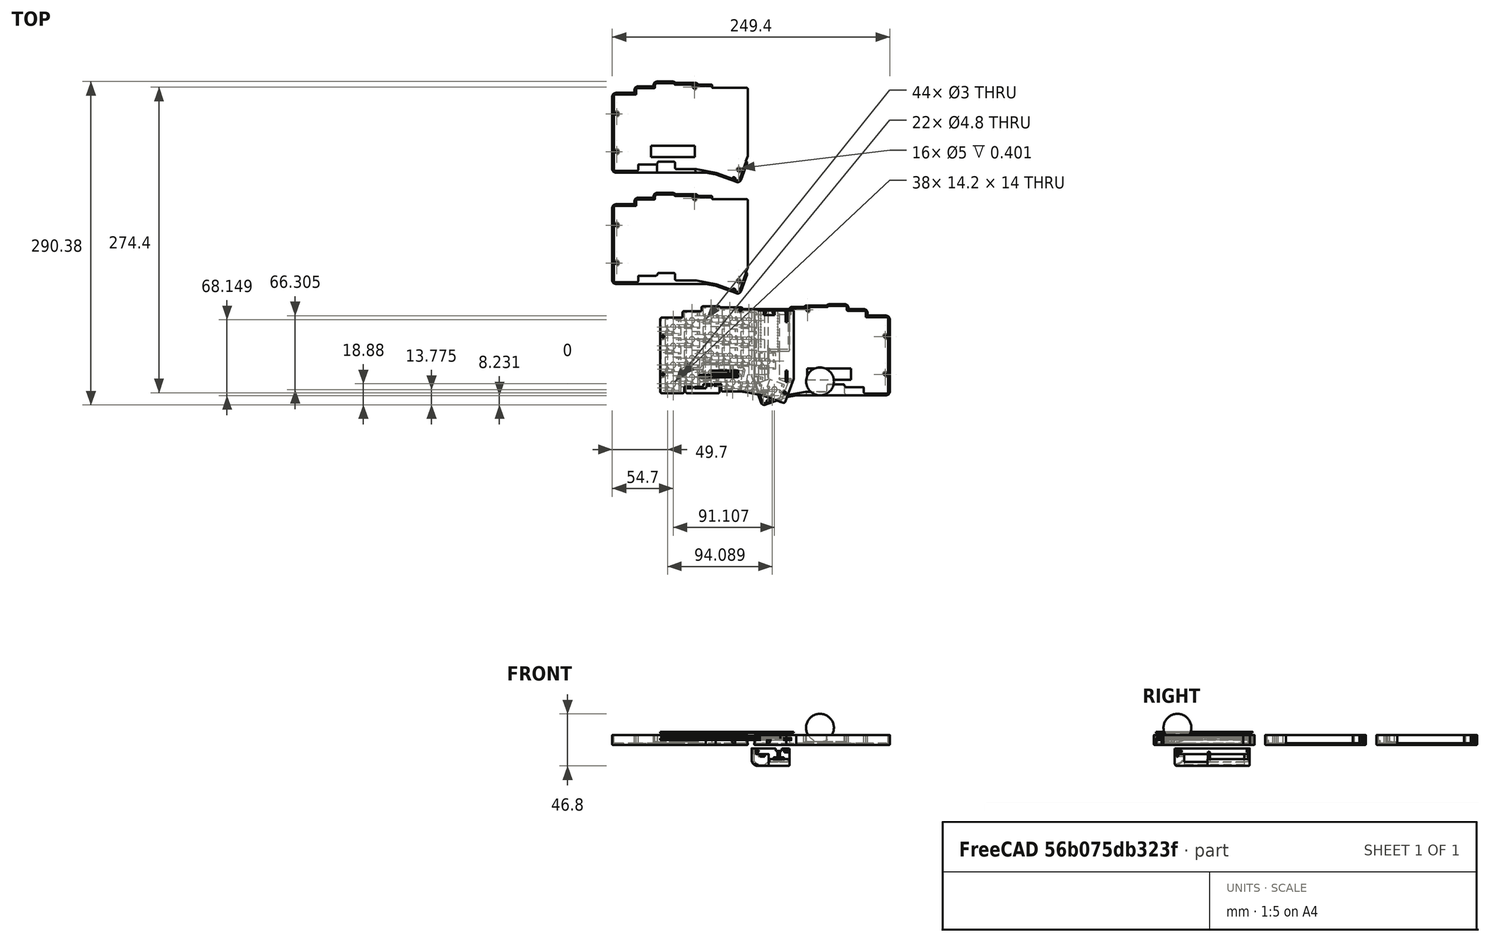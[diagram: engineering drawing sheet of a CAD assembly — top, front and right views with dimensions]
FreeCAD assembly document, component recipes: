
FREECAD ASSEMBLY — COMPONENT RECIPES ("simple-case-xs")

This assembly document has 5 components, labeled P0..P4 below (a component is one placed body or linked part). 4 of them carry a construction recipe — the FreeCAD feature program that regenerates the part from scratch, quoted from this document or its linked companion documents; the rest are supplied as boundary geometry only. No exploded tour is included for this assembly.
NOTE — document 3 of 3 of this assembly tour. The two overview renders and the header above are repeated from document 1; the component sections below continue where the previous document stopped.
COMPONENT P3 — recipe-attached ("case-trackball001", modeled in this document).
Construction recipe (the document's own serialized feature program — sketch geometry with constraints, then the solid features built on it; lengths are millimeters unless a unit is written):

FEATURE [Sketcher::SketchObject] Sketch028  label="top-plate001"
  ArcFitTolerance = 1e-06
  FullyConstrained = true
  MakeInternals = false
  Placement = pos=(0,0,6.6e-15) rot=(0,0,1;0rad)
  sketch-geometry (128):
    g0: ArcOfCircle CenterX=45.3 CenterY=2.4 CenterZ=0 NormalX=-1e-16 NormalY=0 NormalZ=1 AngleXU=1.5708 Radius=1.5 StartAngle=0 EndAngle=1.22777
    g1: LineSegment StartX=59.4 StartY=3.9 StartZ=0 EndX=45.3 EndY=3.9 EndZ=0
    g2: LineSegment StartX=43.8874 StartY=2.9045 StartZ=0 EndX=43.8874 EndY=2.8 EndZ=0
    g3: ArcOfCircle CenterX=59.4 CenterY=2.4 CenterZ=0 NormalX=-1e-16 NormalY=0 NormalZ=1 AngleXU=3.90995e-07 Radius=1.5 StartAngle=0 EndAngle=1.5708
    g4: LineSegment StartX=60.9 StartY=-0.4 StartZ=0 EndX=60.9 EndY=2.4 EndZ=0
    g5: LineSegment StartX=76.4 StartY=-0.4 StartZ=0 EndX=60.9 EndY=-0.4 EndZ=0
    g6: ArcOfCircle CenterX=76.4 CenterY=-1.9 CenterZ=0 NormalX=-1e-16 NormalY=0 NormalZ=1 AngleXU=3.90995e-07 Radius=1.5 StartAngle=0 EndAngle=1.5708
    g7: LineSegment StartX=77.9 StartY=-6.3 StartZ=0 EndX=77.9 EndY=-1.9 EndZ=0
    g8: LineSegment StartX=96.4 StartY=-6.3 StartZ=0 EndX=77.9 EndY=-6.3 EndZ=0
    g9: ArcOfCircle CenterX=96.4 CenterY=-7.8 CenterZ=0 NormalX=-1e-16 NormalY=0 NormalZ=1 AngleXU=3.90995e-07 Radius=1.5 StartAngle=0 EndAngle=1.5708
    g10: LineSegment StartX=97.9 StartY=-59.8 StartZ=0 EndX=97.9 EndY=-7.8 EndZ=0
    g11: LineSegment StartX=97.9 StartY=-72.8 StartZ=0 EndX=97.9 EndY=-59.8 EndZ=0
    g12: ArcOfCircle CenterX=96.4 CenterY=-72.8 CenterZ=0 NormalX=-1e-16 NormalY=0 NormalZ=1 AngleXU=-1.5708 Radius=1.5 StartAngle=0 EndAngle=1.5708
    g13: LineSegment StartX=78 StartY=-74.3 StartZ=0 EndX=96.4 EndY=-74.3 EndZ=0
    g14: ArcOfCircle CenterX=78 CenterY=-72.8 CenterZ=0 NormalX=-1e-16 NormalY=0 NormalZ=1 AngleXU=-3.14159 Radius=1.5 StartAngle=0 EndAngle=1.5708
    g15: LineSegment StartX=76.5 StartY=-68.4 StartZ=0 EndX=76.5 EndY=-72.8 EndZ=0
    g16: LineSegment StartX=60.7 StartY=-68.4 StartZ=0 EndX=76.5 EndY=-68.4 EndZ=0
    g17: ArcOfCircle CenterX=60.7 CenterY=-66.9 CenterZ=0 NormalX=-1e-16 NormalY=0 NormalZ=1 AngleXU=-3.14159 Radius=1.5 StartAngle=0 EndAngle=1.5708
    g18: LineSegment StartX=59.2 StartY=-66.1 StartZ=0 EndX=59.2 EndY=-66.9 EndZ=0
    g19: LineSegment StartX=43.1 StartY=-66.1 StartZ=0 EndX=59.2 EndY=-66.1 EndZ=0
    g20: LineSegment StartX=43.1 StartY=-71.2 StartZ=0 EndX=43.1 EndY=-66.1 EndZ=0
    g21: ArcOfCircle CenterX=41.6 CenterY=-71.2 CenterZ=0 NormalX=-1e-16 NormalY=0 NormalZ=1 AngleXU=-1.5708 Radius=1.5 StartAngle=0 EndAngle=1.5708
    g22: LineSegment StartX=41.4 StartY=-72.7 StartZ=0 EndX=41.6 EndY=-72.7 EndZ=0
    g23: LineSegment StartX=24.227 StartY=-72.7043 StartZ=0 EndX=41.4 EndY=-72.7 EndZ=0
    g24: LineSegment StartX=6.18739 StartY=-75.9853 StartZ=0 EndX=24.227 EndY=-72.7043 EndZ=0
    g25: LineSegment StartX=-12.4977 StartY=-82.7894 StartZ=0 EndX=6.18739 EndY=-75.9853 EndZ=0
    g26: ArcOfCircle CenterX=-13.0109 CenterY=-81.3798 CenterZ=0 NormalX=-1e-16 NormalY=0 NormalZ=1 AngleXU=-2.78723 Radius=1.50005 StartAngle=0 EndAngle=1.56562
    g27: LineSegment StartX=-20.3 StartY=-66 StartZ=0 EndX=-14.4178 EndY=-81.9004 EndZ=0
    g28: LineSegment StartX=-9.1 StartY=-61.9235 StartZ=0 EndX=-20.3 EndY=-66 EndZ=0
    g29: LineSegment StartX=-9.1 StartY=-61 StartZ=0 EndX=-9.1 EndY=-61.9235 EndZ=0
    g30: LineSegment StartX=-9.1 StartY=-36.9 StartZ=0 EndX=-9.1 EndY=-61 EndZ=0
    g31: LineSegment StartX=9.9 StartY=-36.9 StartZ=0 EndX=-9.1 EndY=-36.9 EndZ=0
    g32: LineSegment StartX=9.9 StartY=1.3 StartZ=0 EndX=9.9 EndY=-36.9 EndZ=0
    g33: LineSegment StartX=23.7 StartY=1.3 StartZ=0 EndX=9.9 EndY=1.3 EndZ=0
    g34: ArcOfCircle CenterX=25.2 CenterY=1.3 CenterZ=0 NormalX=-1e-16 NormalY=0 NormalZ=1 AngleXU=1.5708 Radius=1.5 StartAngle=0 EndAngle=1.5708
    g35: LineSegment StartX=43.8874 StartY=2.8 StartZ=0 EndX=25.2 EndY=2.8 EndZ=0
    g36: LineSegment StartX=93.5 StartY=-72.8 StartZ=0 EndX=79.3 EndY=-72.8 EndZ=0
    g37: LineSegment StartX=93.5 StartY=-58.8 StartZ=0 EndX=93.5 EndY=-72.8 EndZ=0
    g38: LineSegment StartX=79.3 StartY=-58.8 StartZ=0 EndX=93.5 EndY=-58.8 EndZ=0
    g39: LineSegment StartX=79.3 StartY=-72.8 StartZ=0 EndX=79.3 EndY=-58.8 EndZ=0
    g40: LineSegment StartX=76.5 StartY=-66.85 StartZ=0 EndX=62.3 EndY=-66.85 EndZ=0
    g41: LineSegment StartX=76.5 StartY=-52.85 StartZ=0 EndX=76.5 EndY=-66.85 EndZ=0
    g42: LineSegment StartX=62.3 StartY=-52.85 StartZ=0 EndX=76.5 EndY=-52.85 EndZ=0
    g43: LineSegment StartX=62.3 StartY=-66.85 StartZ=0 EndX=62.3 EndY=-52.85 EndZ=0
    g44: Circle CenterX=95.6 CenterY=-57.3 CenterZ=0 NormalX=-1e-16 NormalY=0 NormalZ=1 AngleXU=-1.5708 Radius=1.1
    g45: LineSegment StartX=93.5 StartY=-55.8 StartZ=0 EndX=79.3 EndY=-55.8 EndZ=0
    g46: LineSegment StartX=93.5 StartY=-41.8 StartZ=0 EndX=93.5 EndY=-55.8 EndZ=0
    g47: LineSegment StartX=79.3 StartY=-41.8 StartZ=0 EndX=93.5 EndY=-41.8 EndZ=0
    g48: LineSegment StartX=79.3 StartY=-55.8 StartZ=0 EndX=79.3 EndY=-41.8 EndZ=0
    g49: LineSegment StartX=76.5 StartY=-49.85 StartZ=0 EndX=62.3 EndY=-49.85 EndZ=0
    g50: LineSegment StartX=76.5 StartY=-35.85 StartZ=0 EndX=76.5 EndY=-49.85 EndZ=0
    g51: LineSegment StartX=62.3 StartY=-35.85 StartZ=0 EndX=76.5 EndY=-35.85 EndZ=0
    g52: LineSegment StartX=62.3 StartY=-49.85 StartZ=0 EndX=62.3 EndY=-35.85 EndZ=0
    g53: LineSegment StartX=59.5 StartY=-62.6 StartZ=0 EndX=45.3 EndY=-62.6 EndZ=0
    g54: LineSegment StartX=59.5 StartY=-48.6 StartZ=0 EndX=59.5 EndY=-62.6 EndZ=0
    g55: LineSegment StartX=45.3 StartY=-48.6 StartZ=0 EndX=59.5 EndY=-48.6 EndZ=0
    g56: LineSegment StartX=45.3 StartY=-62.6 StartZ=0 EndX=45.3 EndY=-48.6 EndZ=0
    g57: LineSegment StartX=39.95 StartY=-71.1 StartZ=0 EndX=25.75 EndY=-71.1 EndZ=0
    g58: LineSegment StartX=39.95 StartY=-57.1 StartZ=0 EndX=39.95 EndY=-71.1 EndZ=0
    g59: LineSegment StartX=25.75 StartY=-57.1 StartZ=0 EndX=39.95 EndY=-57.1 EndZ=0
    g60: LineSegment StartX=25.75 StartY=-71.1 StartZ=0 EndX=25.75 EndY=-57.1 EndZ=0
    g61: LineSegment StartX=21.8608 StartY=-71.3659 StartZ=0 EndX=7.87653 EndY=-73.8317 EndZ=0
    g62: LineSegment StartX=19.4297 StartY=-57.5786 StartZ=0 EndX=21.8608 EndY=-71.3659 EndZ=0
    g63: LineSegment StartX=5.44545 StartY=-60.0444 StartZ=0 EndX=19.4297 EndY=-57.5786 EndZ=0
    g64: LineSegment StartX=7.87653 StartY=-73.8317 StartZ=0 EndX=5.44545 EndY=-60.0444 EndZ=0
    g65: LineSegment StartX=4.35879 StartY=-75.0546 StartZ=0 EndX=-8.98485 EndY=-79.9113 EndZ=0
    g66: LineSegment StartX=-0.429495 StartY=-61.8989 StartZ=0 EndX=4.35879 EndY=-75.0546 EndZ=0
    g67: LineSegment StartX=-13.7731 StartY=-66.7556 StartZ=0 EndX=-0.429495 EndY=-61.8989 EndZ=0
    g68: LineSegment StartX=-8.98485 StartY=-79.9113 StartZ=0 EndX=-13.7731 EndY=-66.7556 EndZ=0
    g69: Circle CenterX=-14 CenterY=-73.8 CenterZ=0 NormalX=-1e-16 NormalY=0 NormalZ=1 AngleXU=-1.5708 Radius=1.1
    g70: LineSegment StartX=42.5 StartY=-47.725 StartZ=0 EndX=28.3 EndY=-47.725 EndZ=0
    g71: LineSegment StartX=42.5 StartY=-33.725 StartZ=0 EndX=42.5 EndY=-47.725 EndZ=0
    g72: LineSegment StartX=28.3 StartY=-33.725 StartZ=0 EndX=42.5 EndY=-33.725 EndZ=0
    g73: LineSegment StartX=28.3 StartY=-47.725 StartZ=0 EndX=28.3 EndY=-33.725 EndZ=0
    g74: LineSegment StartX=25.5 StartY=-49.85 StartZ=0 EndX=11.3 EndY=-49.85 EndZ=0
    g75: LineSegment StartX=25.5 StartY=-35.85 StartZ=0 EndX=25.5 EndY=-49.85 EndZ=0
    g76: LineSegment StartX=11.3 StartY=-35.85 StartZ=0 EndX=25.5 EndY=-35.85 EndZ=0
    g77: LineSegment StartX=11.3 StartY=-49.85 StartZ=0 EndX=11.3 EndY=-35.85 EndZ=0
    g78: LineSegment StartX=8.5 StartY=-52.4 StartZ=0 EndX=-5.7 EndY=-52.4 EndZ=0
    g79: LineSegment StartX=8.5 StartY=-38.4 StartZ=0 EndX=8.5 EndY=-52.4 EndZ=0
    g80: LineSegment StartX=-5.7 StartY=-38.4 StartZ=0 EndX=8.5 EndY=-38.4 EndZ=0
    g81: LineSegment StartX=-5.7 StartY=-52.4 StartZ=0 EndX=-5.7 EndY=-38.4 EndZ=0
    g82: LineSegment StartX=93.5 StartY=-38.8 StartZ=0 EndX=79.3 EndY=-38.8 EndZ=0
    g83: LineSegment StartX=93.5 StartY=-24.8 StartZ=0 EndX=93.5 EndY=-38.8 EndZ=0
    g84: LineSegment StartX=79.3 StartY=-24.8 StartZ=0 EndX=93.5 EndY=-24.8 EndZ=0
    g85: LineSegment StartX=79.3 StartY=-38.8 StartZ=0 EndX=79.3 EndY=-24.8 EndZ=0
    g86: Circle CenterX=95.6 CenterY=-23.3 CenterZ=0 NormalX=-1e-16 NormalY=0 NormalZ=1 AngleXU=-1.5708 Radius=1.1
    g87: LineSegment StartX=76.5 StartY=-32.85 StartZ=0 EndX=62.3 EndY=-32.85 EndZ=0
    g88: LineSegment StartX=76.5 StartY=-18.85 StartZ=0 EndX=76.5 EndY=-32.85 EndZ=0
    g89: LineSegment StartX=62.3 StartY=-18.85 StartZ=0 EndX=76.5 EndY=-18.85 EndZ=0
    g90: LineSegment StartX=62.3 StartY=-32.85 StartZ=0 EndX=62.3 EndY=-18.85 EndZ=0
    g91: LineSegment StartX=59.5 StartY=-45.6 StartZ=0 EndX=45.3 EndY=-45.6 EndZ=0
    g92: LineSegment StartX=59.5 StartY=-31.6 StartZ=0 EndX=59.5 EndY=-45.6 EndZ=0
    g93: LineSegment StartX=45.3 StartY=-31.6 StartZ=0 EndX=59.5 EndY=-31.6 EndZ=0
    g94: LineSegment StartX=45.3 StartY=-45.6 StartZ=0 EndX=45.3 EndY=-31.6 EndZ=0
    g95: LineSegment StartX=59.5 StartY=-28.6 StartZ=0 EndX=45.3 EndY=-28.6 EndZ=0
    g96: LineSegment StartX=59.5 StartY=-14.6 StartZ=0 EndX=59.5 EndY=-28.6 EndZ=0
    g97: LineSegment StartX=45.3 StartY=-14.6 StartZ=0 EndX=59.5 EndY=-14.6 EndZ=0
    g98: LineSegment StartX=45.3 StartY=-28.6 StartZ=0 EndX=45.3 EndY=-14.6 EndZ=0
    g99: LineSegment StartX=93.5 StartY=-21.8 StartZ=0 EndX=79.3 EndY=-21.8 EndZ=0
    g100: LineSegment StartX=93.5 StartY=-7.8 StartZ=0 EndX=93.5 EndY=-21.8 EndZ=0
    g101: LineSegment StartX=79.3 StartY=-7.8 StartZ=0 EndX=93.5 EndY=-7.8 EndZ=0
    g102: LineSegment StartX=79.3 StartY=-21.8 StartZ=0 EndX=79.3 EndY=-7.8 EndZ=0
    g103: LineSegment StartX=76.5 StartY=-15.85 StartZ=0 EndX=62.3 EndY=-15.85 EndZ=0
    g104: LineSegment StartX=76.5 StartY=-1.85 StartZ=0 EndX=76.5 EndY=-15.85 EndZ=0
    g105: LineSegment StartX=62.3 StartY=-1.85 StartZ=0 EndX=76.5 EndY=-1.85 EndZ=0
    g106: LineSegment StartX=62.3 StartY=-15.85 StartZ=0 EndX=62.3 EndY=-1.85 EndZ=0
    g107: LineSegment StartX=59.5 StartY=-11.6 StartZ=0 EndX=45.3 EndY=-11.6 EndZ=0
    g108: LineSegment StartX=59.5 StartY=2.4 StartZ=0 EndX=59.5 EndY=-11.6 EndZ=0
    g109: LineSegment StartX=45.3 StartY=2.4 StartZ=0 EndX=59.5 EndY=2.4 EndZ=0
    g110: LineSegment StartX=45.3 StartY=-11.6 StartZ=0 EndX=45.3 EndY=2.4 EndZ=0
    g111: LineSegment StartX=42.5 StartY=-30.725 StartZ=0 EndX=28.3 EndY=-30.725 EndZ=0
    g112: LineSegment StartX=42.5 StartY=-16.725 StartZ=0 EndX=42.5 EndY=-30.725 EndZ=0
    g113: LineSegment StartX=28.3 StartY=-16.725 StartZ=0 EndX=42.5 EndY=-16.725 EndZ=0
    g114: LineSegment StartX=28.3 StartY=-30.725 StartZ=0 EndX=28.3 EndY=-16.725 EndZ=0
    g115: LineSegment StartX=25.5 StartY=-32.85 StartZ=0 EndX=11.3 EndY=-32.85 EndZ=0
    g116: LineSegment StartX=25.5 StartY=-18.85 StartZ=0 EndX=25.5 EndY=-32.85 EndZ=0
    g117: LineSegment StartX=11.3 StartY=-18.85 StartZ=0 EndX=25.5 EndY=-18.85 EndZ=0
    g118: LineSegment StartX=11.3 StartY=-32.85 StartZ=0 EndX=11.3 EndY=-18.85 EndZ=0
    g119: LineSegment StartX=25.5 StartY=-15.85 StartZ=0 EndX=11.3 EndY=-15.85 EndZ=0
    g120: LineSegment StartX=25.5 StartY=-1.85 StartZ=0 EndX=25.5 EndY=-15.85 EndZ=0
    g121: LineSegment StartX=11.3 StartY=-1.85 StartZ=0 EndX=25.5 EndY=-1.85 EndZ=0
    g122: LineSegment StartX=11.3 StartY=-15.85 StartZ=0 EndX=11.3 EndY=-1.85 EndZ=0
    g123: LineSegment StartX=42.5 StartY=-13.725 StartZ=0 EndX=28.3 EndY=-13.725 EndZ=0
    g124: LineSegment StartX=42.5 StartY=0.275 StartZ=0 EndX=42.5 EndY=-13.725 EndZ=0
    g125: LineSegment StartX=28.3 StartY=0.275 StartZ=0 EndX=42.5 EndY=0.275 EndZ=0
    g126: LineSegment StartX=28.3 StartY=-13.725 StartZ=0 EndX=28.3 EndY=0.275 EndZ=0
    g127: Circle CenterX=25.9 CenterY=0.6 CenterZ=0 NormalX=-1e-16 NormalY=0 NormalZ=1 AngleXU=-1.5708 Radius=1.1
  constraints (252):
    c: Block(g0)
    c: Block(g1)
    c: Block(g2)
    c: Block(g3)
    c: Block(g4)
    c: Block(g5)
    c: Block(g6)
    c: Block(g7)
    c: Block(g8)
    c: Block(g9)
    c: Block(g10)
    c: Block(g11)
    c: Block(g12)
    c: Block(g13)
    c: Block(g14)
    c: Block(g15)
    c: Block(g16)
    c: Block(g17)
    c: Block(g18)
    c: Block(g19)
    c: Block(g20)
    c: Block(g21)
    c: Block(g22)
    c: Block(g23)
    c: Block(g24)
    c: Block(g25)
    c: Block(g26)
    c: Block(g27)
    c: Block(g28)
    c: Block(g29)
    c: Block(g30)
    c: Block(g31)
    c: Block(g32)
    c: Block(g33)
    c: Block(g34)
    c: Block(g35)
    c: Block(g36)
    c: Block(g37)
    c: Block(g38)
    c: Block(g39)
    c: Block(g40)
    c: Block(g41)
    c: Block(g42)
    c: Block(g43)
    c: Block(g44)
    c: Block(g45)
    c: Block(g46)
    c: Block(g47)
    c: Block(g48)
    c: Block(g49)
    c: Block(g50)
    c: Block(g51)
    c: Block(g52)
    c: Block(g53)
    c: Block(g54)
    c: Block(g55)
    c: Block(g56)
    c: Block(g57)
    c: Block(g58)
    c: Block(g59)
    c: Block(g60)
    c: Block(g61)
    c: Block(g62)
    c: Block(g63)
    c: Block(g64)
    c: Block(g65)
    c: Block(g66)
    c: Block(g67)
    c: Block(g68)
    c: Block(g69)
    c: Block(g70)
    c: Block(g71)
    c: Block(g72)
    c: Block(g73)
    c: Block(g74)
    c: Block(g75)
    c: Block(g76)
    c: Block(g77)
    c: Block(g78)
    c: Block(g79)
    c: Block(g80)
    c: Block(g81)
    c: Block(g82)
    c: Block(g83)
    c: Block(g84)
    c: Block(g85)
    c: Block(g86)
    c: Block(g87)
    c: Block(g88)
    c: Block(g89)
    c: Block(g90)
    c: Block(g91)
    c: Block(g92)
    c: Block(g93)
    c: Block(g94)
    c: Block(g95)
    c: Block(g96)
    c: Block(g97)
    c: Block(g98)
    c: Block(g99)
    c: Block(g100)
    c: Block(g101)
    c: Block(g102)
    c: Block(g103)
    c: Block(g104)
    c: Block(g105)
    c: Block(g106)
    c: Block(g107)
    c: Block(g108)
    c: Block(g109)
    c: Block(g110)
    c: Block(g111)
    c: Block(g112)
    c: Block(g113)
    c: Block(g114)
    c: Block(g115)
    c: Block(g116)
    c: Block(g117)
    c: Block(g118)
    c: Block(g119)
    c: Block(g120)
    c: Block(g121)
    c: Block(g122)
    c: Block(g123)
    c: Block(g124)
    c: Block(g125)
    c: Block(g126)
    c: Block(g127)
    c: Coincident(g27,g28)
    c: Coincident(g26,g27)
    c: Coincident(g67,g68)
    c: Coincident(g25,g26)
    c: Coincident(g28,g29)
    c: Coincident(g29,g30)
    c: Coincident(g30,g31)
    c: Coincident(g65,g68)
    c: Coincident(g78,g81)
    c: Coincident(g80,g81)
    c: Coincident(g66,g67)
    c: Coincident(g65,g66)
    c: Coincident(g63,g64)
    c: Coincident(g24,g25)
    c: Coincident(g61,g64)
    c: Coincident(g78,g79)
    c: Coincident(g79,g80)
    c: Coincident(g31,g32)
    c: Coincident(g32,g33)
    c: Coincident(g74,g77)
    c: Coincident(g76,g77)
    c: Coincident(g115,g118)
    c: Coincident(g117,g118)
    c: Coincident(g119,g122)
    c: Coincident(g121,g122)
    c: Coincident(g62,g63)
    c: Coincident(g61,g62)
    c: Coincident(g33,g34)
    c: Coincident(g23,g24)
    c: Coincident(g34,g35)
    c: Coincident(g74,g75)
    c: Coincident(g75,g76)
    c: Coincident(g115,g116)
    c: Coincident(g116,g117)
    c: Coincident(g119,g120)
    c: Coincident(g120,g121)
    c: Coincident(g57,g60)
    c: Coincident(g59,g60)
    c: Coincident(g70,g73)
    c: Coincident(g72,g73)
    c: Coincident(g111,g114)
    c: Coincident(g113,g114)
    c: Coincident(g123,g126)
    c: Coincident(g125,g126)
    c: Coincident(g57,g58)
    c: Coincident(g58,g59)
    c: Coincident(g22,g23)
    c: Coincident(g21,g22)
    c: Coincident(g70,g71)
    c: Coincident(g71,g72)
    c: Coincident(g111,g112)
    c: Coincident(g112,g113)
    c: Coincident(g123,g124)
    c: Coincident(g124,g125)
    c: Coincident(g20,g21)
    c: Coincident(g19,g20)
    c: Coincident(g2,g35)
    c: Coincident(g0,g2)
    c: Coincident(g53,g56)
    c: Coincident(g55,g56)
    c: Coincident(g91,g94)
    c: Coincident(g93,g94)
    c: Coincident(g95,g98)
    c: Coincident(g97,g98)
    c: Coincident(g107,g110)
    c: Coincident(g109,g110)
    c: Coincident(g0,g1)
    c: Coincident(g17,g18)
    c: Coincident(g18,g19)
    c: Coincident(g1,g3)
    c: Coincident(g53,g54)
    c: Coincident(g54,g55)
    c: Coincident(g91,g92)
    c: Coincident(g92,g93)
    c: Coincident(g95,g96)
    c: Coincident(g96,g97)
    c: Coincident(g107,g108)
    c: Coincident(g108,g109)
    c: Coincident(g16,g17)
    c: Coincident(g4,g5)
    c: Coincident(g3,g4)
    c: Coincident(g40,g43)
    c: Coincident(g42,g43)
    c: Coincident(g49,g52)
    c: Coincident(g51,g52)
    c: Coincident(g87,g90)
    c: Coincident(g89,g90)
    c: Coincident(g103,g106)
    c: Coincident(g105,g106)
    c: Coincident(g5,g6)
    c: Coincident(g14,g15)
    c: Coincident(g15,g16)
    c: Coincident(g40,g41)
    c: Coincident(g41,g42)
    c: Coincident(g49,g50)
    c: Coincident(g50,g51)
    c: Coincident(g87,g88)
    c: Coincident(g88,g89)
    c: Coincident(g103,g104)
    c: Coincident(g104,g105)
    c: Coincident(g7,g8)
    c: Coincident(g6,g7)
    c: Coincident(g13,g14)
    c: Coincident(g36,g39)
    c: Coincident(g38,g39)
    c: Coincident(g45,g48)
    c: Coincident(g47,g48)
    c: Coincident(g82,g85)
    c: Coincident(g84,g85)
    c: Coincident(g99,g102)
    c: Coincident(g101,g102)
    c: Coincident(g36,g37)
    c: Coincident(g37,g38)
    c: Coincident(g45,g46)
    c: Coincident(g46,g47)
    c: Coincident(g82,g83)
    c: Coincident(g83,g84)
    c: Coincident(g99,g100)
    c: Coincident(g100,g101)
    c: Coincident(g12,g13)
    c: Coincident(g8,g9)
    c: Coincident(g11,g12)
    c: Coincident(g10,g11)
    c: Coincident(g9,g10)
FEATURE [Sketcher::SketchObject] Sketch029
  ArcFitTolerance = 1e-06
  AttachmentOffset = pos=(0,0,-5.1) rot=(0,0,1;0rad)
  AttachmentSupport = -> [XY_Plane005]
  FullyConstrained = false
  MakeInternals = false
  MapMode = 5
  Placement = pos=(0,0,-5.1) rot=(0,0,1;0rad)
  sketch-geometry (61):
    g0: ArcOfCircle [constr] CenterX=45.3 CenterY=2.4 CenterZ=0 NormalX=-1e-16 NormalY=0 NormalZ=1 AngleXU=1.5708 Radius=1.5 StartAngle=0 EndAngle=1.22777
    g1: LineSegment [constr] StartX=59.4 StartY=3.9 StartZ=0 EndX=45.3 EndY=3.9 EndZ=0
    g2: LineSegment [constr] StartX=43.8874 StartY=2.9045 StartZ=0 EndX=43.8874 EndY=2.8 EndZ=0
    g3: ArcOfCircle [constr] CenterX=59.4 CenterY=2.4 CenterZ=0 NormalX=-1e-16 NormalY=0 NormalZ=1 AngleXU=3.90995e-07 Radius=1.5 StartAngle=0 EndAngle=1.5708
    g4: LineSegment [constr] StartX=60.9 StartY=-0.4 StartZ=0 EndX=60.9 EndY=2.4 EndZ=0
    g5: LineSegment [constr] StartX=76.4 StartY=-0.4 StartZ=0 EndX=60.9 EndY=-0.4 EndZ=0
    g6: ArcOfCircle [constr] CenterX=76.4 CenterY=-1.9 CenterZ=0 NormalX=-1e-16 NormalY=0 NormalZ=1 AngleXU=3.90995e-07 Radius=1.5 StartAngle=0 EndAngle=1.5708
    g7: LineSegment [constr] StartX=77.9 StartY=-6.3 StartZ=0 EndX=77.9 EndY=-1.9 EndZ=0
    g8: LineSegment [constr] StartX=96.4 StartY=-6.3 StartZ=0 EndX=77.9 EndY=-6.3 EndZ=0
    g9: ArcOfCircle [constr] CenterX=96.4 CenterY=-7.8 CenterZ=0 NormalX=-1e-16 NormalY=0 NormalZ=1 AngleXU=3.90995e-07 Radius=1.5 StartAngle=0 EndAngle=1.5708
    g10: LineSegment [constr] StartX=97.9 StartY=-59.8 StartZ=0 EndX=97.9 EndY=-7.8 EndZ=0
    g11: LineSegment [constr] StartX=97.9 StartY=-72.8 StartZ=0 EndX=97.9 EndY=-59.8 EndZ=0
    g12: ArcOfCircle [constr] CenterX=96.4 CenterY=-72.8 CenterZ=0 NormalX=-1e-16 NormalY=0 NormalZ=1 AngleXU=-1.5708 Radius=1.5 StartAngle=0 EndAngle=1.5708
    g13: LineSegment [constr] StartX=78 StartY=-74.3 StartZ=0 EndX=96.4 EndY=-74.3 EndZ=0
    g14: LineSegment [constr] StartX=6.18739 StartY=-75.9853 StartZ=0 EndX=15.4535 EndY=-74.3 EndZ=0
    g15: LineSegment [constr] StartX=-12.4977 StartY=-82.7894 StartZ=0 EndX=6.18739 EndY=-75.9853 EndZ=0
    g16: ArcOfCircle [constr] CenterX=-13.0109 CenterY=-81.3798 CenterZ=0 NormalX=-1e-16 NormalY=0 NormalZ=1 AngleXU=-2.78723 Radius=1.50005 StartAngle=0 EndAngle=1.56562
    g17: LineSegment [constr] StartX=-20.3 StartY=-66 StartZ=0 EndX=-14.4178 EndY=-81.9004 EndZ=0
    g18: LineSegment [constr] StartX=-9.1 StartY=-61.9235 StartZ=0 EndX=-20.3 EndY=-66 EndZ=0
    g19: LineSegment [constr] StartX=-9.1 StartY=-61 StartZ=0 EndX=-9.1 EndY=-61.9235 EndZ=0
    g20: LineSegment [constr] StartX=-9.1 StartY=-36.9 StartZ=0 EndX=-9.1 EndY=-61 EndZ=0
    g21: LineSegment [constr] StartX=9.9 StartY=-36.9 StartZ=0 EndX=-9.1 EndY=-36.9 EndZ=0
    g22: LineSegment [constr] StartX=9.9 StartY=1.3 StartZ=0 EndX=9.9 EndY=-36.9 EndZ=0
    g23: LineSegment [constr] StartX=23.7 StartY=1.3 StartZ=0 EndX=9.9 EndY=1.3 EndZ=0
    g24: ArcOfCircle [constr] CenterX=25.2 CenterY=1.3 CenterZ=0 NormalX=-1e-16 NormalY=0 NormalZ=1 AngleXU=1.5708 Radius=1.5 StartAngle=0 EndAngle=1.5708
    g25: LineSegment [constr] StartX=43.8874 StartY=2.8 StartZ=0 EndX=25.2 EndY=2.8 EndZ=0
    g26: LineSegment [constr] StartX=78 StartY=-74.3 StartZ=0 EndX=15.4535 EndY=-74.3 EndZ=0
    g27: LineSegment StartX=78 StartY=-76.1 StartZ=0 EndX=15.6159 EndY=-76.1 EndZ=0
    g28: LineSegment StartX=6.65976 StartY=-77.7289 StartZ=0 EndX=15.6159 EndY=-76.1 EndZ=0
    g29: LineSegment StartX=-11.8818 StartY=-84.4807 StartZ=0 EndX=6.65976 EndY=-77.7289 EndZ=0
    g30: ArcOfCircle CenterX=-13.0109 CenterY=-81.3798 CenterZ=0 NormalX=0 NormalY=0 NormalZ=1 AngleXU=-2.78723 Radius=3.30007 StartAngle=6.28318 EndAngle=7.84881
    g31: LineSegment StartX=-21.9882 StartY=-66.6245 StartZ=0 EndX=-16.106 EndY=-82.5249 EndZ=0
    g32: LineSegment [constr] StartX=-10.9 StartY=-60.6632 StartZ=0 EndX=-20.9156 EndY=-64.3086 EndZ=0
    g33: LineSegment [constr] StartX=-10.9 StartY=-36.9 StartZ=0 EndX=-10.9 EndY=-60.6632 EndZ=0
    g34: ArcOfCircle [constr] CenterX=-9.1 CenterY=-36.9 CenterZ=0 NormalX=0 NormalY=0 NormalZ=1 AngleXU=0 Radius=1.8 StartAngle=1.5708 EndAngle=3.14159
    g35: LineSegment [constr] StartX=8.1 StartY=-35.1 StartZ=0 EndX=-9.1 EndY=-35.1 EndZ=0
    g36: LineSegment [constr] StartX=8.1 StartY=1.3 StartZ=0 EndX=8.1 EndY=-35.1 EndZ=0
    g37: ArcOfCircle [constr] CenterX=9.9 CenterY=1.3 CenterZ=0 NormalX=0 NormalY=0 NormalZ=1 AngleXU=0 Radius=1.8 StartAngle=1.5708 EndAngle=3.14159
    g38: LineSegment [constr] StartX=22.4341 StartY=3.1 StartZ=0 EndX=9.9 EndY=3.1 EndZ=0
    g39: ArcOfCircle CenterX=25.2 CenterY=1.3 CenterZ=0 NormalX=0 NormalY=0 NormalZ=1 AngleXU=1.5708 Radius=3.3 StartAngle=0 EndAngle=0.993864
    g40: LineSegment StartX=42.8403 StartY=4.6 StartZ=0 EndX=25.2 EndY=4.6 EndZ=0
    g41: ArcOfCircle CenterX=45.3 CenterY=2.4 CenterZ=0 NormalX=0 NormalY=0 NormalZ=1 AngleXU=1.5708 Radius=3.3 StartAngle=0 EndAngle=0.841069
    g42: LineSegment StartX=59.4 StartY=5.7 StartZ=0 EndX=45.3 EndY=5.7 EndZ=0
    g43: ArcOfCircle CenterX=59.4 CenterY=2.4 CenterZ=0 NormalX=0 NormalY=0 NormalZ=1 AngleXU=3.90995e-07 Radius=3.3 StartAngle=-1.8e-15 EndAngle=1.5708
    g44: LineSegment StartX=62.7 StartY=1.4 StartZ=0 EndX=62.7 EndY=2.4 EndZ=0
    g45: LineSegment StartX=76.4 StartY=1.4 StartZ=0 EndX=62.7 EndY=1.4 EndZ=0
    g46: ArcOfCircle CenterX=76.4 CenterY=-1.9 CenterZ=0 NormalX=0 NormalY=0 NormalZ=1 AngleXU=3.90995e-07 Radius=3.3 StartAngle=-1.8e-15 EndAngle=1.5708
    g47: LineSegment StartX=79.7 StartY=-4.5 StartZ=0 EndX=79.7 EndY=-1.9 EndZ=0
    g48: LineSegment StartX=96.4 StartY=-4.5 StartZ=0 EndX=79.7 EndY=-4.5 EndZ=0
    g49: ArcOfCircle CenterX=96.4 CenterY=-7.8 CenterZ=0 NormalX=0 NormalY=0 NormalZ=1 AngleXU=3.90995e-07 Radius=3.3 StartAngle=-1.8e-15 EndAngle=1.5708
    g50: LineSegment StartX=99.7 StartY=-59.8 StartZ=0 EndX=99.7 EndY=-7.8 EndZ=0
    g51: LineSegment StartX=99.7 StartY=-72.8 StartZ=0 EndX=99.7 EndY=-59.8 EndZ=0
    g52: ArcOfCircle CenterX=96.4 CenterY=-72.8 CenterZ=0 NormalX=0 NormalY=0 NormalZ=1 AngleXU=-1.5708 Radius=3.3 StartAngle=0 EndAngle=1.5708
    g53: LineSegment StartX=78 StartY=-76.1 StartZ=0 EndX=96.4 EndY=-76.1 EndZ=0
    g54: LineSegment [constr] StartX=8.1 StartY=1.3 StartZ=0 EndX=8.1 EndY=0 EndZ=0
    g55: LineSegment StartX=8.1 StartY=0 StartZ=0 EndX=-22.1 EndY=0 EndZ=0
    g56: LineSegment StartX=-22.1 StartY=0 StartZ=0 EndX=-22.1 EndY=-61.0545 EndZ=0
    g57: LineSegment StartX=-22.1 StartY=-61.0545 StartZ=0 EndX=-20.3 EndY=-66 EndZ=0
    g58: LineSegment StartX=-20.3 StartY=-66 StartZ=0 EndX=-21.9882 EndY=-66.6245 EndZ=0
    g59: LineSegment StartX=22.4341 StartY=3.1 StartZ=0 EndX=8.1 EndY=3.1 EndZ=0
    g60: LineSegment StartX=8.1 StartY=3.1 StartZ=0 EndX=8.1 EndY=0 EndZ=0
  constraints (101):
    c: Block(g0)
    c: Block(g1)
    c: Block(g2)
    c: Block(g3)
    c: Block(g4)
    c: Block(g5)
    c: Block(g6)
    c: Block(g7)
    c: Block(g8)
    c: Block(g9)
    c: Block(g10)
    c: Block(g11)
    c: Block(g12)
    c: Block(g13)
    c: Block(g14)
    c: Block(g15)
    c: Block(g16)
    c: Block(g17)
    c: Block(g18)
    c: Block(g19)
    c: Block(g20)
    c: Block(g21)
    c: Block(g22)
    c: Block(g23)
    c: Block(g24)
    c: Block(g25)
    c: Coincident(g17,g18)
    c: Coincident(g16,g17)
    c: Coincident(g15,g16)
    c: Coincident(g18,g19)
    c: Coincident(g19,g20)
    c: Coincident(g20,g21)
    c: Coincident(g14,g15)
    c: Coincident(g21,g22)
    c: Coincident(g22,g23)
    c: Coincident(g23,g24)
    c: Coincident(g24,g25)
    c: Coincident(g2,g25)
    c: Coincident(g0,g2)
    c: Coincident(g0,g1)
    c: Coincident(g1,g3)
    c: Coincident(g4,g5)
    c: Coincident(g3,g4)
    c: Coincident(g5,g6)
    c: Coincident(g7,g8)
    c: Coincident(g6,g7)
    c: Coincident(g12,g13)
    c: Coincident(g8,g9)
    c: Coincident(g11,g12)
    c: Coincident(g10,g11)
    c: Coincident(g9,g10)
    c: Coincident(g26,g13)
    c: Horizontal(g26)
    c: Coincident(g14,g26)
    c: Coincident(g27,g28)
    c: Coincident(g27,g53)
    c: Coincident(g28,g29)
    c: Coincident(g32,g33)
    c: Tangent(g33,g34) = -1.5708
    c: Tangent(g34,g35) = -1.5708
    c: Coincident(g35,g36)
    c: Tangent(g36,g37) = -1.5708
    c: Tangent(g37,g38) = -1.5708
    c: Coincident(g38,g39)
    c: Coincident(g40,g41)
    c: Coincident(g44,g45)
    c: Coincident(g47,g48)
    c: Coincident(g50,g51)
    c: Coincident(g54,g36)
    c: PointOnObject(g54,g-1)
    c: Vertical(g54)
    c: Coincident(g55,g54)
    c: PointOnObject(g55,g-1)
    c: Coincident(g56,g55)
    c: Vertical(g56)
    c: DistanceX(g55,g-1) = 22.1
    c: Coincident(g57,g56)
    c: Coincident(g57,g17)
    c: Angle(g18,g57) = 1.5708
    c: Coincident(g58,g17)
    c: Coincident(g58,g31)
    c: Coincident(g30,g31)
    c: Coincident(g29,g30)
    c: Coincident(g39,g40)
    c: Coincident(g41,g42)
    c: Coincident(g42,g43)
    c: Coincident(g43,g44)
    c: Coincident(g45,g46)
    c: Coincident(g46,g47)
    c: Coincident(g52,g53)
    c: Coincident(g48,g49)
    c: Coincident(g51,g52)
    c: Coincident(g49,g50)
    c: Block(g38)
    c: Block(g36)
    c: Coincident(g59,g38)
    c: Horizontal(g59)
    c: Tangent(g59,g37)
    c: Coincident(g60,g59)
    c: Coincident(g60,g54)
    c: Vertical(g60)
FEATURE [PartDesign::Pad] Pad011
  Direction = (0,0,1)
  Length = 7.3
  Length2 = 1.5
  Profile = -> Sketch029
  ReferenceAxis = -> Sketch029 [N_Axis]
  Refine = true
  Suppressed = false
  Type = 4
FEATURE [Sketcher::SketchObject] Sketch030  label="bottom-plate001"
  ArcFitTolerance = 1e-06
  FullyConstrained = true
  MakeInternals = false
  Placement = pos=(0,0,6.6e-15) rot=(0,0,1;0rad)
  sketch-geometry (74):
    g0: ArcOfCircle CenterX=45.3 CenterY=2.4 CenterZ=0 NormalX=-1e-16 NormalY=0 NormalZ=1 AngleXU=1.5708 Radius=1.5 StartAngle=0 EndAngle=1.22777
    g1: LineSegment StartX=59.4 StartY=3.9 StartZ=0 EndX=45.3 EndY=3.9 EndZ=0
    g2: LineSegment StartX=43.8874 StartY=2.9045 StartZ=0 EndX=43.8874 EndY=2.8 EndZ=0
    g3: ArcOfCircle CenterX=59.4 CenterY=2.4 CenterZ=0 NormalX=-1e-16 NormalY=0 NormalZ=1 AngleXU=3.90995e-07 Radius=1.5 StartAngle=0 EndAngle=1.5708
    g4: LineSegment StartX=60.9 StartY=-0.4 StartZ=0 EndX=60.9 EndY=2.4 EndZ=0
    g5: LineSegment StartX=76.4 StartY=-0.4 StartZ=0 EndX=60.9 EndY=-0.4 EndZ=0
    g6: ArcOfCircle CenterX=76.4 CenterY=-1.9 CenterZ=0 NormalX=-1e-16 NormalY=0 NormalZ=1 AngleXU=3.90995e-07 Radius=1.5 StartAngle=0 EndAngle=1.5708
    g7: LineSegment StartX=77.9 StartY=-6.3 StartZ=0 EndX=77.9 EndY=-1.9 EndZ=0
    g8: LineSegment StartX=96.4 StartY=-6.3 StartZ=0 EndX=77.9 EndY=-6.3 EndZ=0
    g9: ArcOfCircle CenterX=96.4 CenterY=-7.8 CenterZ=0 NormalX=-1e-16 NormalY=0 NormalZ=1 AngleXU=3.90995e-07 Radius=1.5 StartAngle=0 EndAngle=1.5708
    g10: LineSegment StartX=97.9 StartY=-59.8 StartZ=0 EndX=97.9 EndY=-7.8 EndZ=0
    g11: LineSegment StartX=97.9 StartY=-72.8 StartZ=0 EndX=97.9 EndY=-59.8 EndZ=0
    g12: ArcOfCircle CenterX=96.4 CenterY=-72.8 CenterZ=0 NormalX=-1e-16 NormalY=0 NormalZ=1 AngleXU=-1.5708 Radius=1.5 StartAngle=0 EndAngle=1.5708
    g13: LineSegment StartX=78 StartY=-74.3 StartZ=0 EndX=96.4 EndY=-74.3 EndZ=0
    g14: ArcOfCircle CenterX=78 CenterY=-72.8 CenterZ=0 NormalX=-1e-16 NormalY=0 NormalZ=1 AngleXU=-3.14159 Radius=1.5 StartAngle=0 EndAngle=1.5708
    g15: LineSegment StartX=76.5 StartY=-68.4 StartZ=0 EndX=76.5 EndY=-72.8 EndZ=0
    g16: LineSegment StartX=68.6 StartY=-68.4 StartZ=0 EndX=76.5 EndY=-68.4 EndZ=0
    g17: LineSegment StartX=68.6 StartY=-69.9 StartZ=0 EndX=68.6 EndY=-68.4 EndZ=0
    g18: LineSegment StartX=75 StartY=-69.9 StartZ=0 EndX=68.6 EndY=-69.9 EndZ=0
    g19: LineSegment StartX=75 StartY=-72.8 StartZ=0 EndX=75 EndY=-69.9 EndZ=0
    g20: ArcOfCircle CenterX=73.5 CenterY=-72.8 CenterZ=0 NormalX=-1e-16 NormalY=0 NormalZ=1 AngleXU=-1.5708 Radius=1.5 StartAngle=0 EndAngle=1.5708
    g21: LineSegment StartX=46.1 StartY=-74.3 StartZ=0 EndX=73.5 EndY=-74.3 EndZ=0
    g22: ArcOfCircle CenterX=46.1 CenterY=-72.8 CenterZ=0 NormalX=-1e-16 NormalY=0 NormalZ=1 AngleXU=-3.14159 Radius=1.5 StartAngle=0 EndAngle=1.5708
    g23: LineSegment StartX=44.6 StartY=-67.6 StartZ=0 EndX=44.6 EndY=-72.8 EndZ=0
    g24: LineSegment StartX=49.65 StartY=-67.6 StartZ=0 EndX=44.6 EndY=-67.6 EndZ=0
    g25: LineSegment StartX=49.65 StartY=-66.1 StartZ=0 EndX=49.65 EndY=-67.6 EndZ=0
    g26: LineSegment StartX=43.1 StartY=-66.1 StartZ=0 EndX=49.65 EndY=-66.1 EndZ=0
    g27: LineSegment StartX=43.1 StartY=-71.2 StartZ=0 EndX=43.1 EndY=-66.1 EndZ=0
    g28: ArcOfCircle CenterX=41.6 CenterY=-71.2 CenterZ=0 NormalX=-1e-16 NormalY=0 NormalZ=1 AngleXU=-1.5708 Radius=1.5 StartAngle=0 EndAngle=1.5708
    g29: LineSegment StartX=41.4 StartY=-72.7 StartZ=0 EndX=41.6 EndY=-72.7 EndZ=0
    g30: LineSegment StartX=24.227 StartY=-72.7043 StartZ=0 EndX=41.4 EndY=-72.7 EndZ=0
    g31: LineSegment StartX=6.18739 StartY=-75.9853 StartZ=0 EndX=24.227 EndY=-72.7043 EndZ=0
    g32: LineSegment StartX=-12.4977 StartY=-82.7894 StartZ=0 EndX=6.18739 EndY=-75.9853 EndZ=0
    g33: ArcOfCircle CenterX=-13.011 CenterY=-81.3799 CenterZ=0 NormalX=-1e-16 NormalY=0 NormalZ=1 AngleXU=-2.78726 Radius=1.5 StartAngle=0 EndAngle=1.56568
    g34: LineSegment StartX=-22.1 StartY=-61.1344 StartZ=0 EndX=-14.4178 EndY=-81.9004 EndZ=0
    g35: LineSegment StartX=-22.1 StartY=0 StartZ=0 EndX=-22.1 EndY=-61.1344 EndZ=0
    g36: LineSegment StartX=-16.4 StartY=0 StartZ=0 EndX=-22.1 EndY=0 EndZ=0
    g37: LineSegment StartX=-16.4 StartY=-10.5 StartZ=0 EndX=-16.4 EndY=0 EndZ=0
    g38: LineSegment StartX=-14.8 StartY=-10.5 StartZ=0 EndX=-16.4 EndY=-10.5 EndZ=0
    g39: LineSegment StartX=-14.8 StartY=0 StartZ=0 EndX=-14.8 EndY=-10.5 EndZ=0
    g40: LineSegment StartX=-5 StartY=0 StartZ=0 EndX=-14.8 EndY=0 EndZ=0
    g41: LineSegment StartX=-5 StartY=-4 StartZ=0 EndX=-5 EndY=0 EndZ=0
    g42: LineSegment StartX=5 StartY=-4 StartZ=0 EndX=-5 EndY=-4 EndZ=0
    g43: LineSegment StartX=5 StartY=0 StartZ=0 EndX=5 EndY=-4 EndZ=0
    g44: LineSegment StartX=9.9 StartY=0 StartZ=0 EndX=5 EndY=0 EndZ=0
    g45: LineSegment StartX=9.9 StartY=1.3 StartZ=0 EndX=9.9 EndY=0 EndZ=0
    g46: LineSegment StartX=23.7 StartY=1.3 StartZ=0 EndX=9.9 EndY=1.3 EndZ=0
    g47: ArcOfCircle CenterX=25.2 CenterY=1.3 CenterZ=0 NormalX=-1e-16 NormalY=0 NormalZ=1 AngleXU=1.5708 Radius=1.5 StartAngle=0 EndAngle=1.5708
    g48: LineSegment StartX=43.8874 StartY=2.8 StartZ=0 EndX=25.2 EndY=2.8 EndZ=0
    g49: Circle CenterX=95.6 CenterY=-57.3 CenterZ=0 NormalX=-1e-16 NormalY=0 NormalZ=1 AngleXU=-1.5708 Radius=1.1
    g50: ArcOfCircle CenterX=60.7 CenterY=-66.9 CenterZ=0 NormalX=-1e-16 NormalY=0 NormalZ=1 AngleXU=-3.14159 Radius=1.5 StartAngle=0 EndAngle=1.5708
    g51: LineSegment StartX=59.2 StartY=-66.1 StartZ=0 EndX=59.2 EndY=-66.9 EndZ=0
    g52: LineSegment StartX=51.15 StartY=-66.1 StartZ=0 EndX=59.2 EndY=-66.1 EndZ=0
    g53: LineSegment StartX=51.15 StartY=-67.6 StartZ=0 EndX=51.15 EndY=-66.1 EndZ=0
    g54: LineSegment StartX=56.7 StartY=-67.6 StartZ=0 EndX=51.15 EndY=-67.6 EndZ=0
    g55: LineSegment StartX=56.7 StartY=-69.9 StartZ=0 EndX=56.7 EndY=-67.6 EndZ=0
    g56: LineSegment StartX=67.1 StartY=-69.9 StartZ=0 EndX=56.7 EndY=-69.9 EndZ=0
    g57: LineSegment StartX=67.1 StartY=-68.4 StartZ=0 EndX=67.1 EndY=-69.9 EndZ=0
    g58: LineSegment StartX=60.7 StartY=-68.4 StartZ=0 EndX=67.1 EndY=-68.4 EndZ=0
    g59: LineSegment StartX=62.7 StartY=-60 StartZ=0 EndX=27.8 EndY=-60 EndZ=0
    g60: LineSegment StartX=62.7 StartY=-57.6 StartZ=0 EndX=62.7 EndY=-60 EndZ=0
    g61: LineSegment StartX=27.8 StartY=-57.6 StartZ=0 EndX=62.7 EndY=-57.6 EndZ=0
    g62: LineSegment StartX=27.8 StartY=-60 StartZ=0 EndX=27.8 EndY=-57.6 EndZ=0
    g63: Circle CenterX=-14 CenterY=-73.8 CenterZ=0 NormalX=-1e-16 NormalY=0 NormalZ=1 AngleXU=-1.5708 Radius=1.1
    g64: LineSegment StartX=-14.8 StartY=-64.1 StartZ=0 EndX=-16.4 EndY=-64.1 EndZ=0
    g65: LineSegment StartX=-14.8 StartY=-54 StartZ=0 EndX=-14.8 EndY=-64.1 EndZ=0
    g66: LineSegment StartX=-16.4 StartY=-54 StartZ=0 EndX=-14.8 EndY=-54 EndZ=0
    g67: LineSegment StartX=-16.4 StartY=-64.1 StartZ=0 EndX=-16.4 EndY=-54 EndZ=0
    g68: LineSegment StartX=52 StartY=-56.2 StartZ=0 EndX=27.8 EndY=-56.2 EndZ=0
    g69: LineSegment StartX=52 StartY=-53.8 StartZ=0 EndX=52 EndY=-56.2 EndZ=0
    g70: LineSegment StartX=27.8 StartY=-53.8 StartZ=0 EndX=52 EndY=-53.8 EndZ=0
    g71: LineSegment StartX=27.8 StartY=-56.2 StartZ=0 EndX=27.8 EndY=-53.8 EndZ=0
    g72: Circle CenterX=95.6 CenterY=-23.3 CenterZ=0 NormalX=-1e-16 NormalY=0 NormalZ=1 AngleXU=-1.5708 Radius=1.1
    g73: Circle CenterX=25.9 CenterY=0.6 CenterZ=0 NormalX=-1e-16 NormalY=0 NormalZ=1 AngleXU=-1.5708 Radius=1.1
  constraints (144):
    c: Coincident(g34,g35)
    c: Coincident(g35,g36)
    c: Coincident(g64,g67)
    c: Coincident(g66,g67)
    c: Coincident(g37,g38)
    c: Coincident(g36,g37)
    c: Coincident(g64,g65)
    c: Coincident(g65,g66)
    c: Coincident(g38,g39)
    c: Coincident(g39,g40)
    c: Coincident(g33,g34)
    c: Coincident(g32,g33)
    c: Coincident(g41,g42)
    c: Coincident(g40,g41)
    c: Coincident(g42,g43)
    c: Coincident(g43,g44)
    c: Coincident(g31,g32)
    c: Coincident(g44,g45)
    c: Coincident(g45,g46)
    c: Coincident(g46,g47)
    c: Coincident(g30,g31)
    c: Coincident(g47,g48)
    c: Coincident(g59,g62)
    c: Coincident(g61,g62)
    c: Coincident(g68,g71)
    c: Coincident(g70,g71)
    c: Coincident(g29,g30)
    c: Coincident(g28,g29)
    c: Coincident(g27,g28)
    c: Coincident(g26,g27)
    c: Coincident(g2,g48)
    c: Coincident(g0,g2)
    c: Coincident(g22,g23)
    c: Coincident(g23,g24)
    c: Coincident(g0,g1)
    c: Coincident(g21,g22)
    c: Coincident(g24,g25)
    c: Coincident(g25,g26)
    c: Coincident(g53,g54)
    c: Coincident(g52,g53)
    c: Coincident(g68,g69)
    c: Coincident(g69,g70)
    c: Coincident(g55,g56)
    c: Coincident(g54,g55)
    c: Coincident(g50,g51)
    c: Coincident(g51,g52)
    c: Coincident(g1,g3)
    c: Coincident(g50,g58)
    c: Coincident(g4,g5)
    c: Coincident(g3,g4)
    c: Coincident(g59,g60)
    c: Coincident(g60,g61)
    c: Coincident(g56,g57)
    c: Coincident(g57,g58)
    c: Coincident(g17,g18)
    c: Coincident(g16,g17)
    c: Coincident(g20,g21)
    c: Coincident(g19,g20)
    c: Coincident(g18,g19)
    c: Coincident(g5,g6)
    c: Coincident(g14,g15)
    c: Coincident(g15,g16)
    c: Coincident(g7,g8)
    c: Coincident(g6,g7)
    c: Coincident(g13,g14)
    c: Coincident(g12,g13)
    c: Coincident(g8,g9)
    c: Coincident(g11,g12)
    c: Coincident(g10,g11)
    c: Coincident(g9,g10)
    c: Block(g0)
    c: Block(g1)
    c: Block(g2)
    c: Block(g3)
    c: Block(g4)
    c: Block(g5)
    c: Block(g6)
    c: Block(g7)
    c: Block(g8)
    c: Block(g9)
    c: Block(g10)
    c: Block(g11)
    c: Block(g12)
    c: Block(g13)
    c: Block(g14)
    c: Block(g15)
    c: Block(g16)
    c: Block(g17)
    c: Block(g18)
    c: Block(g19)
    c: Block(g20)
    c: Block(g21)
    c: Block(g22)
    c: Block(g23)
    c: Block(g24)
    c: Block(g25)
    c: Block(g26)
    c: Block(g27)
    c: Block(g28)
    c: Block(g29)
    c: Block(g30)
    c: Block(g31)
    c: Block(g32)
    c: Block(g33)
    c: Block(g34)
    c: Block(g35)
    c: Block(g36)
    c: Block(g37)
    c: Block(g38)
    c: Block(g39)
    c: Block(g40)
    c: Block(g41)
    c: Block(g42)
    c: Block(g43)
    c: Block(g44)
    c: Block(g45)
    c: Block(g46)
    c: Block(g47)
    c: Block(g48)
    c: Block(g49)
    c: Block(g50)
    c: Block(g51)
    c: Block(g52)
    c: Block(g53)
    c: Block(g54)
    c: Block(g55)
    c: Block(g56)
    c: Block(g57)
    c: Block(g58)
    c: Block(g59)
    c: Block(g60)
    c: Block(g61)
    c: Block(g62)
    c: Block(g63)
    c: Block(g64)
    c: Block(g65)
    c: Block(g66)
    c: Block(g67)
    c: Block(g68)
    c: Block(g69)
    c: Block(g70)
    c: Block(g71)
    c: Block(g72)
    c: Block(g73)
FEATURE [Sketcher::SketchObject] Sketch031
  ArcFitTolerance = 1e-06
  AttachmentOffset = pos=(0,0,-5.1) rot=(0,0,1;0rad)
  AttachmentSupport = -> [XY_Plane005]
  FullyConstrained = false
  MakeInternals = false
  MapMode = 5
  Placement = pos=(0,0,-5.1) rot=(0,0,1;0rad)
  sketch-geometry (96):
    g0: ArcOfCircle [constr] CenterX=45.3 CenterY=2.4 CenterZ=0 NormalX=-1e-16 NormalY=0 NormalZ=1 AngleXU=1.5708 Radius=1.5 StartAngle=0 EndAngle=1.22777
    g1: LineSegment [constr] StartX=59.4 StartY=3.9 StartZ=0 EndX=45.3 EndY=3.9 EndZ=0
    g2: LineSegment [constr] StartX=43.8874 StartY=2.9045 StartZ=0 EndX=43.8874 EndY=2.8 EndZ=0
    g3: ArcOfCircle [constr] CenterX=59.4 CenterY=2.4 CenterZ=0 NormalX=-1e-16 NormalY=0 NormalZ=1 AngleXU=3.90995e-07 Radius=1.5 StartAngle=0 EndAngle=1.5708
    g4: LineSegment [constr] StartX=60.9 StartY=-0.4 StartZ=0 EndX=60.9 EndY=2.4 EndZ=0
    g5: LineSegment [constr] StartX=76.4 StartY=-0.4 StartZ=0 EndX=60.9 EndY=-0.4 EndZ=0
    g6: ArcOfCircle [constr] CenterX=76.4 CenterY=-1.9 CenterZ=0 NormalX=-1e-16 NormalY=0 NormalZ=1 AngleXU=3.90995e-07 Radius=1.5 StartAngle=0 EndAngle=1.5708
    g7: LineSegment [constr] StartX=77.9 StartY=-6.3 StartZ=0 EndX=77.9 EndY=-1.9 EndZ=0
    g8: LineSegment [constr] StartX=96.4 StartY=-6.3 StartZ=0 EndX=77.9 EndY=-6.3 EndZ=0
    g9: ArcOfCircle [constr] CenterX=96.4 CenterY=-7.8 CenterZ=0 NormalX=-1e-16 NormalY=0 NormalZ=1 AngleXU=3.90995e-07 Radius=1.5 StartAngle=0 EndAngle=1.5708
    g10: LineSegment [constr] StartX=97.9 StartY=-59.8 StartZ=0 EndX=97.9 EndY=-7.8 EndZ=0
    g11: LineSegment [constr] StartX=97.9 StartY=-72.8 StartZ=0 EndX=97.9 EndY=-59.8 EndZ=0
    g12: ArcOfCircle [constr] CenterX=96.4 CenterY=-72.8 CenterZ=0 NormalX=-1e-16 NormalY=0 NormalZ=1 AngleXU=-1.5708 Radius=1.5 StartAngle=0 EndAngle=1.5708
    g13: LineSegment [constr] StartX=78 StartY=-74.3 StartZ=0 EndX=96.4 EndY=-74.3 EndZ=0
    g14: ArcOfCircle [constr] CenterX=78 CenterY=-72.8 CenterZ=0 NormalX=-1e-16 NormalY=0 NormalZ=1 AngleXU=-3.14159 Radius=1.5 StartAngle=0 EndAngle=1.5708
    g15: LineSegment [constr] StartX=76.5 StartY=-68.4 StartZ=0 EndX=76.5 EndY=-72.8 EndZ=0
    g16: LineSegment [constr] StartX=68.6 StartY=-68.4 StartZ=0 EndX=76.5 EndY=-68.4 EndZ=0
    g17: LineSegment [constr] StartX=43.1 StartY=-66.1 StartZ=0 EndX=49.65 EndY=-66.1 EndZ=0
    g18: LineSegment [constr] StartX=43.1 StartY=-71.2 StartZ=0 EndX=43.1 EndY=-66.1 EndZ=0
    g19: ArcOfCircle [constr] CenterX=41.6 CenterY=-71.2 CenterZ=0 NormalX=-1e-16 NormalY=0 NormalZ=1 AngleXU=-1.5708 Radius=1.5 StartAngle=0 EndAngle=1.5708
    g20: LineSegment [constr] StartX=41.4 StartY=-72.7 StartZ=0 EndX=41.6 EndY=-72.7 EndZ=0
    g21: LineSegment [constr] StartX=24.227 StartY=-72.7043 StartZ=0 EndX=41.4 EndY=-72.7 EndZ=0
    g22: LineSegment [constr] StartX=6.18739 StartY=-75.9853 StartZ=0 EndX=24.227 EndY=-72.7043 EndZ=0
    g23: LineSegment [constr] StartX=-12.4977 StartY=-82.7894 StartZ=0 EndX=6.18739 EndY=-75.9853 EndZ=0
    g24: ArcOfCircle [constr] CenterX=-13.011 CenterY=-81.3799 CenterZ=0 NormalX=-1e-16 NormalY=0 NormalZ=1 AngleXU=-2.78726 Radius=1.5 StartAngle=0 EndAngle=1.56568
    g25: LineSegment [constr] StartX=-22.1 StartY=-61.1344 StartZ=0 EndX=-14.4178 EndY=-81.9004 EndZ=0
    g26: LineSegment [constr] StartX=-22.1 StartY=0 StartZ=0 EndX=-22.1 EndY=-61.1344 EndZ=0
    g27: LineSegment [constr] StartX=9.9 StartY=0 StartZ=0 EndX=5 EndY=0 EndZ=0
    g28: LineSegment [constr] StartX=9.9 StartY=1.3 StartZ=0 EndX=9.9 EndY=0 EndZ=0
    g29: LineSegment [constr] StartX=23.7 StartY=1.3 StartZ=0 EndX=9.9 EndY=1.3 EndZ=0
    g30: ArcOfCircle [constr] CenterX=25.2 CenterY=1.3 CenterZ=0 NormalX=-1e-16 NormalY=0 NormalZ=1 AngleXU=1.5708 Radius=1.5 StartAngle=0 EndAngle=1.5708
    g31: LineSegment [constr] StartX=43.8874 StartY=2.8 StartZ=0 EndX=25.2 EndY=2.8 EndZ=0
    g32: Circle [constr] CenterX=95.6 CenterY=-57.3 CenterZ=0 NormalX=-1e-16 NormalY=0 NormalZ=1 AngleXU=-1.5708 Radius=1.1
    g33: ArcOfCircle [constr] CenterX=60.7 CenterY=-66.9 CenterZ=0 NormalX=-1e-16 NormalY=0 NormalZ=1 AngleXU=-3.14159 Radius=1.5 StartAngle=0 EndAngle=1.5708
    g34: LineSegment [constr] StartX=59.2 StartY=-66.1 StartZ=0 EndX=59.2 EndY=-66.9 EndZ=0
    g35: LineSegment [constr] StartX=51.15 StartY=-66.1 StartZ=0 EndX=59.2 EndY=-66.1 EndZ=0
    g36: LineSegment [constr] StartX=60.7 StartY=-68.4 StartZ=0 EndX=67.1 EndY=-68.4 EndZ=0
    g37: LineSegment [constr] StartX=62.7 StartY=-60 StartZ=0 EndX=27.8 EndY=-60 EndZ=0
    g38: LineSegment [constr] StartX=62.7 StartY=-57.6 StartZ=0 EndX=62.7 EndY=-60 EndZ=0
    g39: LineSegment [constr] StartX=27.8 StartY=-57.6 StartZ=0 EndX=62.7 EndY=-57.6 EndZ=0
    g40: LineSegment [constr] StartX=27.8 StartY=-60 StartZ=0 EndX=27.8 EndY=-57.6 EndZ=0
    g41: Circle [constr] CenterX=-14 CenterY=-73.8 CenterZ=0 NormalX=-1e-16 NormalY=0 NormalZ=1 AngleXU=-1.5708 Radius=1.1
    g42: LineSegment [constr] StartX=-14.8 StartY=-64.1 StartZ=0 EndX=-16.4 EndY=-64.1 EndZ=0
    g43: LineSegment [constr] StartX=-14.8 StartY=-54 StartZ=0 EndX=-14.8 EndY=-64.1 EndZ=0
    g44: LineSegment [constr] StartX=-16.4 StartY=-54 StartZ=0 EndX=-14.8 EndY=-54 EndZ=0
    g45: LineSegment [constr] StartX=-16.4 StartY=-64.1 StartZ=0 EndX=-16.4 EndY=-54 EndZ=0
    g46: LineSegment [constr] StartX=52 StartY=-56.2 StartZ=0 EndX=27.8 EndY=-56.2 EndZ=0
    g47: LineSegment [constr] StartX=52 StartY=-53.8 StartZ=0 EndX=52 EndY=-56.2 EndZ=0
    g48: LineSegment [constr] StartX=27.8 StartY=-53.8 StartZ=0 EndX=52 EndY=-53.8 EndZ=0
    g49: LineSegment [constr] StartX=27.8 StartY=-56.2 StartZ=0 EndX=27.8 EndY=-53.8 EndZ=0
    g50: Circle [constr] CenterX=95.6 CenterY=-23.3 CenterZ=0 NormalX=-1e-16 NormalY=0 NormalZ=1 AngleXU=-1.5708 Radius=1.1
    g51: Circle [constr] CenterX=25.9 CenterY=0.6 CenterZ=0 NormalX=-1e-16 NormalY=0 NormalZ=1 AngleXU=-1.5708 Radius=1.1
    g52: LineSegment [constr] StartX=49.65 StartY=-66.1 StartZ=0 EndX=51.15 EndY=-66.1 EndZ=0
    g53: LineSegment [constr] StartX=67.1 StartY=-68.4 StartZ=0 EndX=68.6 EndY=-68.4 EndZ=0
    g54: LineSegment [constr] StartX=-22.1 StartY=0 StartZ=0 EndX=5 EndY=0 EndZ=0
    g55: LineSegment StartX=-22.1 StartY=0.3 StartZ=0 EndX=5 EndY=0.3 EndZ=0
    g56: LineSegment StartX=9.6 StartY=0.3 StartZ=0 EndX=5 EndY=0.3 EndZ=0
    g57: LineSegment StartX=9.6 StartY=1.3 StartZ=0 EndX=9.6 EndY=0.3 EndZ=0
    g58: ArcOfCircle CenterX=9.9 CenterY=1.3 CenterZ=0 NormalX=0 NormalY=0 NormalZ=1 AngleXU=0 Radius=0.3 StartAngle=1.5708 EndAngle=3.14159
    g59: LineSegment StartX=23.4252 StartY=1.6 StartZ=0 EndX=9.9 EndY=1.6 EndZ=0
    g60: ArcOfCircle CenterX=25.2 CenterY=1.3 CenterZ=0 NormalX=0 NormalY=0 NormalZ=1 AngleXU=1.5708 Radius=1.8 StartAngle=0 EndAngle=1.40335
    g61: LineSegment StartX=43.6417 StartY=3.1 StartZ=0 EndX=25.2 EndY=3.1 EndZ=0
    g62: ArcOfCircle CenterX=45.3 CenterY=2.4 CenterZ=0 NormalX=0 NormalY=0 NormalZ=1 AngleXU=1.5708 Radius=1.8 StartAngle=0 EndAngle=1.17137
    g63: LineSegment StartX=59.4 StartY=4.2 StartZ=0 EndX=45.3 EndY=4.2 EndZ=0
    g64: ArcOfCircle CenterX=59.4 CenterY=2.4 CenterZ=0 NormalX=0 NormalY=0 NormalZ=1 AngleXU=3.90995e-07 Radius=1.8 StartAngle=-1.8e-15 EndAngle=1.5708
    g65: LineSegment StartX=61.2 StartY=-0.1 StartZ=0 EndX=61.2 EndY=2.4 EndZ=0
    g66: LineSegment StartX=76.4 StartY=-0.1 StartZ=0 EndX=61.2 EndY=-0.1 EndZ=0
    g67: ArcOfCircle CenterX=76.4 CenterY=-1.9 CenterZ=0 NormalX=0 NormalY=0 NormalZ=1 AngleXU=3.90995e-07 Radius=1.8 StartAngle=-1.8e-15 EndAngle=1.5708
    g68: LineSegment StartX=78.2 StartY=-6 StartZ=0 EndX=78.2 EndY=-1.9 EndZ=0
    g69: LineSegment StartX=96.4 StartY=-6 StartZ=0 EndX=78.2 EndY=-6 EndZ=0
    g70: ArcOfCircle CenterX=96.4 CenterY=-7.8 CenterZ=0 NormalX=0 NormalY=0 NormalZ=1 AngleXU=3.90995e-07 Radius=1.8 StartAngle=9e-16 EndAngle=1.5708
    g71: LineSegment StartX=98.2 StartY=-59.8 StartZ=0 EndX=98.2 EndY=-7.8 EndZ=0
    g72: LineSegment StartX=98.2 StartY=-72.8 StartZ=0 EndX=98.2 EndY=-59.8 EndZ=0
    g73: ArcOfCircle CenterX=96.4 CenterY=-72.8 CenterZ=0 NormalX=0 NormalY=0 NormalZ=1 AngleXU=-1.5708 Radius=1.8 StartAngle=0 EndAngle=1.5708
    g74: LineSegment StartX=78 StartY=-74.6 StartZ=0 EndX=96.4 EndY=-74.6 EndZ=0
    g75: ArcOfCircle CenterX=78 CenterY=-72.8 CenterZ=0 NormalX=0 NormalY=0 NormalZ=1 AngleXU=-3.14159 Radius=1.8 StartAngle=0 EndAngle=1.5708
    g76: LineSegment StartX=76.2 StartY=-68.7 StartZ=0 EndX=76.2 EndY=-72.8 EndZ=0
    g77: LineSegment StartX=68.6 StartY=-68.7 StartZ=0 EndX=76.2 EndY=-68.7 EndZ=0
    g78: LineSegment StartX=67.1 StartY=-68.7 StartZ=0 EndX=68.6 EndY=-68.7 EndZ=0
    g79: LineSegment StartX=60.7 StartY=-68.7 StartZ=0 EndX=67.1 EndY=-68.7 EndZ=0
    g80: ArcOfCircle CenterX=60.7 CenterY=-66.9 CenterZ=0 NormalX=0 NormalY=0 NormalZ=1 AngleXU=-3.14159 Radius=1.8 StartAngle=0 EndAngle=1.5708
    g81: LineSegment StartX=58.9 StartY=-66.4 StartZ=0 EndX=58.9 EndY=-66.9 EndZ=0
    g82: LineSegment StartX=51.15 StartY=-66.4 StartZ=0 EndX=58.9 EndY=-66.4 EndZ=0
    g83: LineSegment StartX=49.65 StartY=-66.4 StartZ=0 EndX=51.15 EndY=-66.4 EndZ=0
    g84: LineSegment StartX=43.4 StartY=-66.4 StartZ=0 EndX=49.65 EndY=-66.4 EndZ=0
    g85: LineSegment StartX=43.4 StartY=-71.2 StartZ=0 EndX=43.4 EndY=-66.4 EndZ=0
    g86: ArcOfCircle CenterX=41.6 CenterY=-71.2 CenterZ=0 NormalX=0 NormalY=0 NormalZ=1 AngleXU=-1.5708 Radius=1.8 StartAngle=0 EndAngle=1.5708
    g87: LineSegment StartX=41.4 StartY=-73 StartZ=0 EndX=41.6 EndY=-73 EndZ=0
    g88: LineSegment StartX=24.2541 StartY=-73.0043 StartZ=0 EndX=41.4 EndY=-73 EndZ=0
    g89: LineSegment StartX=6.26611 StartY=-76.2759 StartZ=0 EndX=24.2541 EndY=-73.0043 EndZ=0
    g90: LineSegment StartX=-12.3951 StartY=-83.0713 StartZ=0 EndX=6.26611 EndY=-76.2759 EndZ=0
    g91: ArcOfCircle CenterX=-13.011 CenterY=-81.3799 CenterZ=0 NormalX=0 NormalY=0 NormalZ=1 AngleXU=-2.78726 Radius=1.8 StartAngle=6.28319 EndAngle=7.84887
    g92: LineSegment StartX=-22.3814 StartY=-61.2385 StartZ=0 EndX=-14.6992 EndY=-82.0044 EndZ=0
    g93: ArcOfCircle CenterX=-22.1 CenterY=-61.1344 CenterZ=0 NormalX=0 NormalY=0 NormalZ=1 AngleXU=1.5708 Radius=0.3 StartAngle=1.5708 EndAngle=1.92513
    g94: LineSegment StartX=-22.4 StartY=0 StartZ=0 EndX=-22.4 EndY=-61.1344 EndZ=0
    g95: ArcOfCircle CenterX=-22.1 CenterY=0 CenterZ=0 NormalX=0 NormalY=0 NormalZ=1 AngleXU=0 Radius=0.3 StartAngle=1.5708 EndAngle=3.14159
  constraints (147):
    c: Coincident(g25,g26)
    c: Coincident(g42,g45)
    c: Coincident(g44,g45)
    c: Coincident(g42,g43)
    c: Coincident(g43,g44)
    c: Coincident(g24,g25)
    c: Coincident(g23,g24)
    c: Coincident(g22,g23)
    c: Coincident(g27,g28)
    c: Coincident(g28,g29)
    c: Coincident(g29,g30)
    c: Coincident(g21,g22)
    c: Coincident(g30,g31)
    c: Coincident(g37,g40)
    c: Coincident(g39,g40)
    c: Coincident(g46,g49)
    c: Coincident(g48,g49)
    c: Coincident(g20,g21)
    c: Coincident(g19,g20)
    c: Coincident(g18,g19)
    c: Coincident(g17,g18)
    c: Coincident(g2,g31)
    c: Coincident(g0,g2)
    c: Coincident(g0,g1)
    c: Coincident(g46,g47)
    c: Coincident(g47,g48)
    c: Coincident(g33,g34)
    c: Coincident(g34,g35)
    c: Coincident(g1,g3)
    c: Coincident(g33,g36)
    c: Coincident(g4,g5)
    c: Coincident(g3,g4)
    c: Coincident(g37,g38)
    c: Coincident(g38,g39)
    c: Coincident(g5,g6)
    c: Coincident(g14,g15)
    c: Coincident(g15,g16)
    c: Coincident(g7,g8)
    c: Coincident(g6,g7)
    c: Coincident(g13,g14)
    c: Coincident(g12,g13)
    c: Coincident(g8,g9)
    c: Coincident(g11,g12)
    c: Coincident(g10,g11)
    c: Coincident(g9,g10)
    c: Block(g0)
    c: Block(g1)
    c: Block(g2)
    c: Block(g3)
    c: Block(g4)
    c: Block(g5)
    c: Block(g6)
    c: Block(g7)
    c: Block(g8)
    c: Block(g9)
    c: Block(g10)
    c: Block(g11)
    c: Block(g12)
    c: Block(g13)
    c: Block(g14)
    c: Block(g15)
    c: Block(g16)
    c: Block(g17)
    c: Block(g18)
    c: Block(g19)
    c: Block(g20)
    c: Block(g21)
    c: Block(g22)
    c: Block(g23)
    c: Block(g24)
    c: Block(g25)
    c: Block(g26)
    c: Block(g27)
    c: Block(g28)
    c: Block(g29)
    c: Block(g30)
    c: Block(g31)
    c: Block(g32)
    c: Block(g33)
    c: Block(g34)
    c: Block(g35)
    c: Block(g36)
    c: Block(g37)
    c: Block(g38)
    c: Block(g39)
    c: Block(g40)
    c: Block(g41)
    c: Block(g42)
    c: Block(g43)
    c: Block(g44)
    c: Block(g45)
    c: Block(g46)
    c: Block(g47)
    c: Block(g48)
    c: Block(g49)
    c: Block(g50)
    c: Block(g51)
    c: Coincident(g52,g17)
    c: Coincident(g52,g35)
    c: Horizontal(g52)
    c: Coincident(g53,g36)
    c: Coincident(g53,g16)
    c: Horizontal(g53)
    c: Coincident(g54,g26)
    c: Coincident(g54,g27)
    c: Horizontal(g54)
    c: Coincident(g55,g56)
    c: Tangent(g55,g95) = 1.5708
    c: Coincident(g56,g57)
    c: Tangent(g57,g58) = -1.5708
    c: Tangent(g58,g59) = -1.5708
    c: Coincident(g59,g60)
    c: Coincident(g61,g62)
    c: Coincident(g62,g63)
    c: Coincident(g65,g66)
    c: Coincident(g68,g69)
    c: Coincident(g71,g72)
    c: Coincident(g76,g77)
    c: Coincident(g77,g78)
    c: Coincident(g78,g79)
    c: Coincident(g81,g82)
    c: Coincident(g82,g83)
    c: Coincident(g83,g84)
    c: Coincident(g84,g85)
    c: Coincident(g87,g88)
    c: Coincident(g88,g89)
    c: Coincident(g89,g90)
    c: Tangent(g92,g93) = -1.5708
    c: Tangent(g93,g94) = -1.5708
    c: Tangent(g94,g95) = -1.5708
    c: Coincident(g91,g92)
    c: Coincident(g90,g91)
    c: Coincident(g60,g61)
    c: Coincident(g86,g87)
    c: Coincident(g85,g86)
    c: Coincident(g80,g81)
    c: Coincident(g63,g64)
    c: Coincident(g79,g80)
    c: Coincident(g64,g65)
    c: Coincident(g75,g76)
    c: Coincident(g66,g67)
    c: Coincident(g74,g75)
    c: Coincident(g67,g68)
    c: Coincident(g73,g74)
    c: Coincident(g69,g70)
    c: Coincident(g72,g73)
    c: Coincident(g70,g71)
FEATURE [PartDesign::Pocket] Pocket013
  BaseFeature = -> Pad011
  Direction = (0,0,-1)
  Length = 10
  Length2 = 5
  Profile = -> Sketch031
  ReferenceAxis = -> Sketch031 [N_Axis]
  Refine = true
  Reversed = true
  Suppressed = false
  Type = 0
FEATURE [Sketcher::SketchObject] Sketch032
  ArcFitTolerance = 1e-06
  AttachmentOffset = pos=(0,0,-5.1) rot=(0,0,1;0rad)
  AttachmentSupport = -> [XY_Plane005]
  FullyConstrained = false
  MakeInternals = false
  MapMode = 5
  Placement = pos=(0,0,-5.1) rot=(0,0,1;0rad)
  sketch-geometry (4):
    g0: LineSegment StartX=9.9 StartY=0 StartZ=0 EndX=9.9 EndY=7.12941 EndZ=0
    g1: LineSegment StartX=9.9 StartY=7.12941 StartZ=0 EndX=2.38364 EndY=7.12941 EndZ=0
    g2: LineSegment StartX=2.38364 StartY=7.12941 StartZ=0 EndX=2.38364 EndY=0 EndZ=0
    g3: LineSegment StartX=2.38364 StartY=0 StartZ=0 EndX=9.9 EndY=0 EndZ=0
  constraints (10):
    c: Coincident(g0,g1)
    c: Coincident(g1,g2)
    c: Coincident(g2,g3)
    c: Coincident(g3,g0)
    c: Vertical(g0)
    c: Vertical(g2)
    c: Horizontal(g1)
    c: Horizontal(g3)
    c: DistanceX(g-1,g0) = 9.9
    c: PointOnObject(g2,g-1)
FEATURE [PartDesign::Pocket] Pocket014
  BaseFeature = -> Pocket013
  Direction = (0,0,-1)
  Length = 10
  Length2 = 10
  Profile = -> Sketch032
  ReferenceAxis = -> Sketch032 [N_Axis]
  Refine = true
  Reversed = true
  Suppressed = false
  Type = 4
FEATURE [Sketcher::SketchObject] Sketch033
  ArcFitTolerance = 1e-06
  AttachmentSupport = -> [XY_Plane005]
  FullyConstrained = false
  MakeInternals = false
  MapMode = 5
  sketch-geometry (79):
    g0: ArcOfCircle [constr] CenterX=45.3 CenterY=2.4 CenterZ=0 NormalX=-1e-16 NormalY=0 NormalZ=1 AngleXU=1.5708 Radius=1.5 StartAngle=0 EndAngle=1.22777
    g1: LineSegment [constr] StartX=59.4 StartY=3.9 StartZ=0 EndX=45.3 EndY=3.9 EndZ=0
    g2: LineSegment [constr] StartX=43.8874 StartY=2.9045 StartZ=0 EndX=43.8874 EndY=2.8 EndZ=0
    g3: ArcOfCircle [constr] CenterX=59.4 CenterY=2.4 CenterZ=0 NormalX=-1e-16 NormalY=0 NormalZ=1 AngleXU=3.90995e-07 Radius=1.5 StartAngle=0 EndAngle=1.5708
    g4: LineSegment [constr] StartX=60.9 StartY=-0.4 StartZ=0 EndX=60.9 EndY=2.4 EndZ=0
    g5: LineSegment [constr] StartX=76.4 StartY=-0.4 StartZ=0 EndX=60.9 EndY=-0.4 EndZ=0
    g6: ArcOfCircle [constr] CenterX=76.4 CenterY=-1.9 CenterZ=0 NormalX=-1e-16 NormalY=0 NormalZ=1 AngleXU=3.90995e-07 Radius=1.5 StartAngle=0 EndAngle=1.5708
    g7: LineSegment [constr] StartX=77.9 StartY=-6.3 StartZ=0 EndX=77.9 EndY=-1.9 EndZ=0
    g8: LineSegment [constr] StartX=96.4 StartY=-6.3 StartZ=0 EndX=77.9 EndY=-6.3 EndZ=0
    g9: ArcOfCircle [constr] CenterX=96.4 CenterY=-7.8 CenterZ=0 NormalX=-1e-16 NormalY=0 NormalZ=1 AngleXU=3.90995e-07 Radius=1.5 StartAngle=0 EndAngle=1.5708
    g10: LineSegment [constr] StartX=97.9 StartY=-59.8 StartZ=0 EndX=97.9 EndY=-7.8 EndZ=0
    g11: LineSegment [constr] StartX=97.9 StartY=-72.8 StartZ=0 EndX=97.9 EndY=-59.8 EndZ=0
    g12: ArcOfCircle [constr] CenterX=96.4 CenterY=-72.8 CenterZ=0 NormalX=-1e-16 NormalY=0 NormalZ=1 AngleXU=-1.5708 Radius=1.5 StartAngle=0 EndAngle=1.5708
    g13: LineSegment [constr] StartX=78 StartY=-74.3 StartZ=0 EndX=96.4 EndY=-74.3 EndZ=0
    g14: ArcOfCircle [constr] CenterX=78 CenterY=-72.8 CenterZ=0 NormalX=-1e-16 NormalY=0 NormalZ=1 AngleXU=-3.14159 Radius=1.5 StartAngle=0 EndAngle=1.5708
    g15: LineSegment [constr] StartX=76.5 StartY=-68.4 StartZ=0 EndX=76.5 EndY=-72.8 EndZ=0
    g16: LineSegment [constr] StartX=68.6 StartY=-68.4 StartZ=0 EndX=76.5 EndY=-68.4 EndZ=0
    g17: LineSegment [constr] StartX=68.6 StartY=-69.9 StartZ=0 EndX=68.6 EndY=-68.4 EndZ=0
    g18: LineSegment [constr] StartX=75 StartY=-69.9 StartZ=0 EndX=68.6 EndY=-69.9 EndZ=0
    g19: LineSegment [constr] StartX=75 StartY=-72.8 StartZ=0 EndX=75 EndY=-69.9 EndZ=0
    g20: ArcOfCircle [constr] CenterX=73.5 CenterY=-72.8 CenterZ=0 NormalX=-1e-16 NormalY=0 NormalZ=1 AngleXU=-1.5708 Radius=1.5 StartAngle=0 EndAngle=1.5708
    g21: LineSegment [constr] StartX=46.1 StartY=-74.3 StartZ=0 EndX=73.5 EndY=-74.3 EndZ=0
    g22: ArcOfCircle [constr] CenterX=46.1 CenterY=-72.8 CenterZ=0 NormalX=-1e-16 NormalY=0 NormalZ=1 AngleXU=-3.14159 Radius=1.5 StartAngle=0 EndAngle=1.5708
    g23: LineSegment [constr] StartX=44.6 StartY=-67.6 StartZ=0 EndX=44.6 EndY=-72.8 EndZ=0
    g24: LineSegment [constr] StartX=49.65 StartY=-67.6 StartZ=0 EndX=44.6 EndY=-67.6 EndZ=0
    g25: LineSegment [constr] StartX=49.65 StartY=-66.1 StartZ=0 EndX=49.65 EndY=-67.6 EndZ=0
    g26: LineSegment [constr] StartX=43.1 StartY=-66.1 StartZ=0 EndX=49.65 EndY=-66.1 EndZ=0
    g27: LineSegment [constr] StartX=43.1 StartY=-71.2 StartZ=0 EndX=43.1 EndY=-66.1 EndZ=0
    g28: ArcOfCircle [constr] CenterX=41.6 CenterY=-71.2 CenterZ=0 NormalX=-1e-16 NormalY=0 NormalZ=1 AngleXU=-1.5708 Radius=1.5 StartAngle=0 EndAngle=1.5708
    g29: LineSegment [constr] StartX=41.4 StartY=-72.7 StartZ=0 EndX=41.6 EndY=-72.7 EndZ=0
    g30: LineSegment [constr] StartX=24.227 StartY=-72.7043 StartZ=0 EndX=41.4 EndY=-72.7 EndZ=0
    g31: LineSegment [constr] StartX=6.18739 StartY=-75.9853 StartZ=0 EndX=24.227 EndY=-72.7043 EndZ=0
    g32: LineSegment [constr] StartX=-12.4977 StartY=-82.7894 StartZ=0 EndX=6.18739 EndY=-75.9853 EndZ=0
    g33: ArcOfCircle [constr] CenterX=-13.011 CenterY=-81.3799 CenterZ=0 NormalX=-1e-16 NormalY=0 NormalZ=1 AngleXU=-2.78726 Radius=1.5 StartAngle=0 EndAngle=1.56568
    g34: LineSegment [constr] StartX=-22.1 StartY=-61.1344 StartZ=0 EndX=-14.4178 EndY=-81.9004 EndZ=0
    g35: LineSegment [constr] StartX=-22.1 StartY=0 StartZ=0 EndX=-22.1 EndY=-61.1344 EndZ=0
    g36: LineSegment [constr] StartX=-16.4 StartY=0 StartZ=0 EndX=-22.1 EndY=0 EndZ=0
    g37: LineSegment [constr] StartX=-16.4 StartY=-10.5 StartZ=0 EndX=-16.4 EndY=0 EndZ=0
    g38: LineSegment [constr] StartX=-14.8 StartY=-10.5 StartZ=0 EndX=-16.4 EndY=-10.5 EndZ=0
    g39: LineSegment [constr] StartX=-14.8 StartY=0 StartZ=0 EndX=-14.8 EndY=-10.5 EndZ=0
    g40: LineSegment [constr] StartX=-5 StartY=0 StartZ=0 EndX=-14.8 EndY=0 EndZ=0
    g41: LineSegment [constr] StartX=-5 StartY=-4 StartZ=0 EndX=-5 EndY=0 EndZ=0
    g42: LineSegment [constr] StartX=5 StartY=-4 StartZ=0 EndX=-5 EndY=-4 EndZ=0
    g43: LineSegment [constr] StartX=5 StartY=0 StartZ=0 EndX=5 EndY=-4 EndZ=0
    g44: LineSegment [constr] StartX=9.9 StartY=0 StartZ=0 EndX=5 EndY=0 EndZ=0
    g45: LineSegment [constr] StartX=9.9 StartY=1.3 StartZ=0 EndX=9.9 EndY=0 EndZ=0
    g46: LineSegment [constr] StartX=23.7 StartY=1.3 StartZ=0 EndX=9.9 EndY=1.3 EndZ=0
    g47: ArcOfCircle [constr] CenterX=25.2 CenterY=1.3 CenterZ=0 NormalX=-1e-16 NormalY=0 NormalZ=1 AngleXU=1.5708 Radius=1.5 StartAngle=0 EndAngle=1.5708
    g48: LineSegment [constr] StartX=43.8874 StartY=2.8 StartZ=0 EndX=25.2 EndY=2.8 EndZ=0
    g49: Circle [constr] CenterX=95.6 CenterY=-57.3 CenterZ=0 NormalX=-1e-16 NormalY=0 NormalZ=1 AngleXU=-1.5708 Radius=1.1
    g50: ArcOfCircle [constr] CenterX=60.7 CenterY=-66.9 CenterZ=0 NormalX=-1e-16 NormalY=0 NormalZ=1 AngleXU=-3.14159 Radius=1.5 StartAngle=0 EndAngle=1.5708
    g51: LineSegment [constr] StartX=59.2 StartY=-66.1 StartZ=0 EndX=59.2 EndY=-66.9 EndZ=0
    g52: LineSegment [constr] StartX=51.15 StartY=-66.1 StartZ=0 EndX=59.2 EndY=-66.1 EndZ=0
    g53: LineSegment [constr] StartX=51.15 StartY=-67.6 StartZ=0 EndX=51.15 EndY=-66.1 EndZ=0
    g54: LineSegment [constr] StartX=56.7 StartY=-67.6 StartZ=0 EndX=51.15 EndY=-67.6 EndZ=0
    g55: LineSegment [constr] StartX=56.7 StartY=-69.9 StartZ=0 EndX=56.7 EndY=-67.6 EndZ=0
    g56: LineSegment [constr] StartX=67.1 StartY=-69.9 StartZ=0 EndX=56.7 EndY=-69.9 EndZ=0
    g57: LineSegment [constr] StartX=67.1 StartY=-68.4 StartZ=0 EndX=67.1 EndY=-69.9 EndZ=0
    g58: LineSegment [constr] StartX=60.7 StartY=-68.4 StartZ=0 EndX=67.1 EndY=-68.4 EndZ=0
    g59: LineSegment [constr] StartX=62.7 StartY=-60 StartZ=0 EndX=27.8 EndY=-60 EndZ=0
    g60: LineSegment [constr] StartX=62.7 StartY=-57.6 StartZ=0 EndX=62.7 EndY=-60 EndZ=0
    g61: LineSegment [constr] StartX=27.8 StartY=-57.6 StartZ=0 EndX=62.7 EndY=-57.6 EndZ=0
    g62: LineSegment [constr] StartX=27.8 StartY=-60 StartZ=0 EndX=27.8 EndY=-57.6 EndZ=0
    g63: Circle [constr] CenterX=-14 CenterY=-73.8 CenterZ=0 NormalX=-1e-16 NormalY=0 NormalZ=1 AngleXU=-1.5708 Radius=1.1
    g64: LineSegment [constr] StartX=-14.8 StartY=-64.1 StartZ=0 EndX=-16.4 EndY=-64.1 EndZ=0
    g65: LineSegment [constr] StartX=-14.8 StartY=-54 StartZ=0 EndX=-14.8 EndY=-64.1 EndZ=0
    g66: LineSegment [constr] StartX=-16.4 StartY=-54 StartZ=0 EndX=-14.8 EndY=-54 EndZ=0
    g67: LineSegment [constr] StartX=-16.4 StartY=-64.1 StartZ=0 EndX=-16.4 EndY=-54 EndZ=0
    g68: LineSegment [constr] StartX=52 StartY=-56.2 StartZ=0 EndX=27.8 EndY=-56.2 EndZ=0
    g69: LineSegment [constr] StartX=52 StartY=-53.8 StartZ=0 EndX=52 EndY=-56.2 EndZ=0
    g70: LineSegment [constr] StartX=27.8 StartY=-53.8 StartZ=0 EndX=52 EndY=-53.8 EndZ=0
    g71: LineSegment [constr] StartX=27.8 StartY=-56.2 StartZ=0 EndX=27.8 EndY=-53.8 EndZ=0
    g72: Circle [constr] CenterX=95.6 CenterY=-23.3 CenterZ=0 NormalX=-1e-16 NormalY=0 NormalZ=1 AngleXU=-1.5708 Radius=1.1
    g73: Circle [constr] CenterX=25.9 CenterY=0.6 CenterZ=0 NormalX=-1e-16 NormalY=0 NormalZ=1 AngleXU=-1.5708 Radius=1.1
    g74: Circle CenterX=25.9 CenterY=0.6 CenterZ=0 NormalX=0 NormalY=0 NormalZ=1 AngleXU=0 Radius=1.2
    g75: Circle CenterX=25.9 CenterY=0.6 CenterZ=0 NormalX=0 NormalY=0 NormalZ=1 AngleXU=0 Radius=1.2
    g76: Circle CenterX=95.6 CenterY=-23.3 CenterZ=0 NormalX=0 NormalY=0 NormalZ=1 AngleXU=0 Radius=1.1
    g77: Circle CenterX=95.6 CenterY=-57.3 CenterZ=0 NormalX=0 NormalY=0 NormalZ=1 AngleXU=0 Radius=1.1
    g78: Circle CenterX=-14 CenterY=-73.8 CenterZ=0 NormalX=0 NormalY=0 NormalZ=1 AngleXU=0 Radius=1.2
  constraints (153):
    c: Coincident(g34,g35)
    c: Coincident(g35,g36)
    c: Coincident(g64,g67)
    c: Coincident(g66,g67)
    c: Coincident(g37,g38)
    c: Coincident(g36,g37)
    c: Coincident(g64,g65)
    c: Coincident(g65,g66)
    c: Coincident(g38,g39)
    c: Coincident(g39,g40)
    c: Coincident(g33,g34)
    c: Coincident(g32,g33)
    c: Coincident(g41,g42)
    c: Coincident(g40,g41)
    c: Coincident(g42,g43)
    c: Coincident(g43,g44)
    c: Coincident(g31,g32)
    c: Coincident(g44,g45)
    c: Coincident(g45,g46)
    c: Coincident(g46,g47)
    c: Coincident(g30,g31)
    c: Coincident(g47,g48)
    c: Coincident(g59,g62)
    c: Coincident(g61,g62)
    c: Coincident(g68,g71)
    c: Coincident(g70,g71)
    c: Coincident(g29,g30)
    c: Coincident(g28,g29)
    c: Coincident(g27,g28)
    c: Coincident(g26,g27)
    c: Coincident(g2,g48)
    c: Coincident(g0,g2)
    c: Coincident(g22,g23)
    c: Coincident(g23,g24)
    c: Coincident(g0,g1)
    c: Coincident(g21,g22)
    c: Coincident(g24,g25)
    c: Coincident(g25,g26)
    c: Coincident(g53,g54)
    c: Coincident(g52,g53)
    c: Coincident(g68,g69)
    c: Coincident(g69,g70)
    c: Coincident(g55,g56)
    c: Coincident(g54,g55)
    c: Coincident(g50,g51)
    c: Coincident(g51,g52)
    c: Coincident(g1,g3)
    c: Coincident(g50,g58)
    c: Coincident(g4,g5)
    c: Coincident(g3,g4)
    c: Coincident(g59,g60)
    c: Coincident(g60,g61)
    c: Coincident(g56,g57)
    c: Coincident(g57,g58)
    c: Coincident(g17,g18)
    c: Coincident(g16,g17)
    c: Coincident(g20,g21)
    c: Coincident(g19,g20)
    c: Coincident(g18,g19)
    c: Coincident(g5,g6)
    c: Coincident(g14,g15)
    c: Coincident(g15,g16)
    c: Coincident(g7,g8)
    c: Coincident(g6,g7)
    c: Coincident(g13,g14)
    c: Coincident(g12,g13)
    c: Coincident(g8,g9)
    c: Coincident(g11,g12)
    c: Coincident(g10,g11)
    c: Coincident(g9,g10)
    c: Block(g0)
    c: Block(g1)
    c: Block(g2)
    c: Block(g3)
    c: Block(g4)
    c: Block(g5)
    c: Block(g6)
    c: Block(g7)
    c: Block(g8)
    c: Block(g9)
    c: Block(g10)
    c: Block(g11)
    c: Block(g12)
    c: Block(g13)
    c: Block(g14)
    c: Block(g15)
    c: Block(g16)
    c: Block(g17)
    c: Block(g18)
    c: Block(g19)
    c: Block(g20)
    c: Block(g21)
    c: Block(g22)
    c: Block(g23)
    c: Block(g24)
    c: Block(g25)
    c: Block(g26)
    c: Block(g27)
    c: Block(g28)
    c: Block(g29)
    c: Block(g30)
    c: Block(g31)
    c: Block(g32)
    c: Block(g33)
    c: Block(g34)
    c: Block(g35)
    c: Block(g36)
    c: Block(g37)
    c: Block(g38)
    c: Block(g39)
    c: Block(g40)
    c: Block(g41)
    c: Block(g42)
    c: Block(g43)
    c: Block(g44)
    c: Block(g45)
    c: Block(g46)
    c: Block(g47)
    c: Block(g48)
    c: Block(g49)
    c: Block(g50)
    c: Block(g51)
    c: Block(g52)
    c: Block(g53)
    c: Block(g54)
    c: Block(g55)
    c: Block(g56)
    c: Block(g57)
    c: Block(g58)
    c: Block(g59)
    c: Block(g60)
    c: Block(g61)
    c: Block(g62)
    c: Block(g63)
    c: Block(g64)
    c: Block(g65)
    c: Block(g66)
    c: Block(g67)
    c: Block(g68)
    c: Block(g69)
    c: Block(g70)
    c: Block(g71)
    c: Block(g72)
    c: Block(g73)
    c: Diameter(g75) = 2.4
    c: Coincident(g75,g74)
    c: Equal(g75,g74)
    c: Coincident(g76,g72)
    c: Equal(g76,g72)
    c: Coincident(g77,g49)
    c: Equal(g77,g49)
    c: Diameter(g78) = 2.4
    c: Coincident(g78,g63)
FEATURE [PartDesign::Pocket] Pocket015
  BaseFeature = -> Pocket014
  Direction = (0,0,-1)
  Length = 20
  Length2 = 5
  Profile = -> Sketch033
  ReferenceAxis = -> Sketch033 [N_Axis]
  Refine = true
  Suppressed = false
  Type = 0
FEATURE [PartDesign::Fillet] Fillet004
  Base = -> Pocket015 [Edge102,Edge95,Edge85]
  BaseFeature = -> Pocket015
  Radius = 1
  Refine = true
  SupportTransform = false
  Suppressed = false
  UseAllEdges = false
FEATURE [PartDesign::Fillet] Fillet005
  Base = -> Fillet004 [Edge157,Edge179,Edge180,Edge175,Edge165,Edge168,Edge164,Edge57]
  BaseFeature = -> Fillet004
  Radius = 0.499
  Refine = true
  SupportTransform = false
  Suppressed = false
  UseAllEdges = false
FEATURE [Sketcher::SketchObject] Sketch034
  ArcFitTolerance = 1e-06
  AttachmentOffset = pos=(0,0,-5.1) rot=(0,0,1;0rad)
  AttachmentSupport = -> [XY_Plane005]
  FullyConstrained = true
  MakeInternals = false
  MapMode = 5
  Placement = pos=(0,0,-5.1) rot=(0,0,1;0rad)
  sketch-geometry (4):
    g0: LineSegment StartX=25.5 StartY=-52 StartZ=0 EndX=25.5 EndY=-62 EndZ=0
    g1: LineSegment StartX=25.5 StartY=-62 StartZ=0 EndX=65 EndY=-62 EndZ=0
    g2: LineSegment StartX=65 StartY=-62 StartZ=0 EndX=65 EndY=-52 EndZ=0
    g3: LineSegment StartX=65 StartY=-52 StartZ=0 EndX=25.5 EndY=-52 EndZ=0
  constraints (12):
    c: Coincident(g0,g1)
    c: Coincident(g1,g2)
    c: Coincident(g2,g3)
    c: Coincident(g3,g0)
    c: Vertical(g0)
    c: Vertical(g2)
    c: Horizontal(g1)
    c: Horizontal(g3)
    c: DistanceY(g0,g-1) = 52
    c: DistanceY(g0,g-1) = 62
    c: DistanceX(g-1,g0) = 25.5
    c: DistanceX(g-1,g2) = 65
FEATURE [Sketcher::SketchObject] Sketch035
  ArcFitTolerance = 1e-06
  AttachmentOffset = pos=(0,0,-5.9) rot=(0,0,1;0rad)
  AttachmentSupport = -> [XY_Plane005]
  FullyConstrained = false
  MakeInternals = false
  MapMode = 5
  Placement = pos=(0,0,-5.9) rot=(0,0,1;0rad)
  expr: Constraints[144] = Sketch033.Constraints[144]
  expr: Constraints[151] = Sketch033.Constraints[151]
  sketch-geometry (83):
    g0: ArcOfCircle [constr] CenterX=45.3 CenterY=2.4 CenterZ=0 NormalX=-1e-16 NormalY=0 NormalZ=1 AngleXU=1.5708 Radius=1.5 StartAngle=0 EndAngle=1.22777
    g1: LineSegment [constr] StartX=59.4 StartY=3.9 StartZ=0 EndX=45.3 EndY=3.9 EndZ=0
    g2: LineSegment [constr] StartX=43.8874 StartY=2.9045 StartZ=0 EndX=43.8874 EndY=2.8 EndZ=0
    g3: ArcOfCircle [constr] CenterX=59.4 CenterY=2.4 CenterZ=0 NormalX=-1e-16 NormalY=0 NormalZ=1 AngleXU=3.90995e-07 Radius=1.5 StartAngle=0 EndAngle=1.5708
    g4: LineSegment [constr] StartX=60.9 StartY=-0.4 StartZ=0 EndX=60.9 EndY=2.4 EndZ=0
    g5: LineSegment [constr] StartX=76.4 StartY=-0.4 StartZ=0 EndX=60.9 EndY=-0.4 EndZ=0
    g6: ArcOfCircle [constr] CenterX=76.4 CenterY=-1.9 CenterZ=0 NormalX=-1e-16 NormalY=0 NormalZ=1 AngleXU=3.90995e-07 Radius=1.5 StartAngle=0 EndAngle=1.5708
    g7: LineSegment [constr] StartX=77.9 StartY=-6.3 StartZ=0 EndX=77.9 EndY=-1.9 EndZ=0
    g8: LineSegment [constr] StartX=96.4 StartY=-6.3 StartZ=0 EndX=77.9 EndY=-6.3 EndZ=0
    g9: ArcOfCircle [constr] CenterX=96.4 CenterY=-7.8 CenterZ=0 NormalX=-1e-16 NormalY=0 NormalZ=1 AngleXU=3.90995e-07 Radius=1.5 StartAngle=0 EndAngle=1.5708
    g10: LineSegment [constr] StartX=97.9 StartY=-59.8 StartZ=0 EndX=97.9 EndY=-7.8 EndZ=0
    g11: LineSegment [constr] StartX=97.9 StartY=-72.8 StartZ=0 EndX=97.9 EndY=-59.8 EndZ=0
    g12: ArcOfCircle [constr] CenterX=96.4 CenterY=-72.8 CenterZ=0 NormalX=-1e-16 NormalY=0 NormalZ=1 AngleXU=-1.5708 Radius=1.5 StartAngle=0 EndAngle=1.5708
    g13: LineSegment [constr] StartX=78 StartY=-74.3 StartZ=0 EndX=96.4 EndY=-74.3 EndZ=0
    g14: ArcOfCircle [constr] CenterX=78 CenterY=-72.8 CenterZ=0 NormalX=-1e-16 NormalY=0 NormalZ=1 AngleXU=-3.14159 Radius=1.5 StartAngle=0 EndAngle=1.5708
    g15: LineSegment [constr] StartX=76.5 StartY=-68.4 StartZ=0 EndX=76.5 EndY=-72.8 EndZ=0
    g16: LineSegment [constr] StartX=68.6 StartY=-68.4 StartZ=0 EndX=76.5 EndY=-68.4 EndZ=0
    g17: LineSegment [constr] StartX=68.6 StartY=-69.9 StartZ=0 EndX=68.6 EndY=-68.4 EndZ=0
    g18: LineSegment [constr] StartX=75 StartY=-69.9 StartZ=0 EndX=68.6 EndY=-69.9 EndZ=0
    g19: LineSegment [constr] StartX=75 StartY=-72.8 StartZ=0 EndX=75 EndY=-69.9 EndZ=0
    g20: ArcOfCircle [constr] CenterX=73.5 CenterY=-72.8 CenterZ=0 NormalX=-1e-16 NormalY=0 NormalZ=1 AngleXU=-1.5708 Radius=1.5 StartAngle=0 EndAngle=1.5708
    g21: LineSegment [constr] StartX=46.1 StartY=-74.3 StartZ=0 EndX=73.5 EndY=-74.3 EndZ=0
    g22: ArcOfCircle [constr] CenterX=46.1 CenterY=-72.8 CenterZ=0 NormalX=-1e-16 NormalY=0 NormalZ=1 AngleXU=-3.14159 Radius=1.5 StartAngle=0 EndAngle=1.5708
    g23: LineSegment [constr] StartX=44.6 StartY=-67.6 StartZ=0 EndX=44.6 EndY=-72.8 EndZ=0
    g24: LineSegment [constr] StartX=49.65 StartY=-67.6 StartZ=0 EndX=44.6 EndY=-67.6 EndZ=0
    g25: LineSegment [constr] StartX=49.65 StartY=-66.1 StartZ=0 EndX=49.65 EndY=-67.6 EndZ=0
    g26: LineSegment [constr] StartX=43.1 StartY=-66.1 StartZ=0 EndX=49.65 EndY=-66.1 EndZ=0
    g27: LineSegment [constr] StartX=43.1 StartY=-71.2 StartZ=0 EndX=43.1 EndY=-66.1 EndZ=0
    g28: ArcOfCircle [constr] CenterX=41.6 CenterY=-71.2 CenterZ=0 NormalX=-1e-16 NormalY=0 NormalZ=1 AngleXU=-1.5708 Radius=1.5 StartAngle=0 EndAngle=1.5708
    g29: LineSegment [constr] StartX=41.4 StartY=-72.7 StartZ=0 EndX=41.6 EndY=-72.7 EndZ=0
    g30: LineSegment [constr] StartX=24.227 StartY=-72.7043 StartZ=0 EndX=41.4 EndY=-72.7 EndZ=0
    g31: LineSegment [constr] StartX=6.18739 StartY=-75.9853 StartZ=0 EndX=24.227 EndY=-72.7043 EndZ=0
    g32: LineSegment [constr] StartX=-12.4977 StartY=-82.7894 StartZ=0 EndX=6.18739 EndY=-75.9853 EndZ=0
    g33: ArcOfCircle [constr] CenterX=-13.011 CenterY=-81.3799 CenterZ=0 NormalX=-1e-16 NormalY=0 NormalZ=1 AngleXU=-2.78726 Radius=1.5 StartAngle=0 EndAngle=1.56568
    g34: LineSegment [constr] StartX=-22.1 StartY=-61.1344 StartZ=0 EndX=-14.4178 EndY=-81.9004 EndZ=0
    g35: LineSegment [constr] StartX=-22.1 StartY=0 StartZ=0 EndX=-22.1 EndY=-61.1344 EndZ=0
    g36: LineSegment [constr] StartX=-16.4 StartY=0 StartZ=0 EndX=-22.1 EndY=0 EndZ=0
    g37: LineSegment [constr] StartX=-16.4 StartY=-10.5 StartZ=0 EndX=-16.4 EndY=0 EndZ=0
    g38: LineSegment [constr] StartX=-14.8 StartY=-10.5 StartZ=0 EndX=-16.4 EndY=-10.5 EndZ=0
    g39: LineSegment [constr] StartX=-14.8 StartY=0 StartZ=0 EndX=-14.8 EndY=-10.5 EndZ=0
    g40: LineSegment [constr] StartX=-5 StartY=0 StartZ=0 EndX=-14.8 EndY=0 EndZ=0
    g41: LineSegment [constr] StartX=-5 StartY=-4 StartZ=0 EndX=-5 EndY=0 EndZ=0
    g42: LineSegment [constr] StartX=5 StartY=-4 StartZ=0 EndX=-5 EndY=-4 EndZ=0
    g43: LineSegment [constr] StartX=5 StartY=0 StartZ=0 EndX=5 EndY=-4 EndZ=0
    g44: LineSegment [constr] StartX=9.9 StartY=0 StartZ=0 EndX=5 EndY=0 EndZ=0
    g45: LineSegment [constr] StartX=9.9 StartY=1.3 StartZ=0 EndX=9.9 EndY=0 EndZ=0
    g46: LineSegment [constr] StartX=23.7 StartY=1.3 StartZ=0 EndX=9.9 EndY=1.3 EndZ=0
    g47: ArcOfCircle [constr] CenterX=25.2 CenterY=1.3 CenterZ=0 NormalX=-1e-16 NormalY=0 NormalZ=1 AngleXU=1.5708 Radius=1.5 StartAngle=0 EndAngle=1.5708
    g48: LineSegment [constr] StartX=43.8874 StartY=2.8 StartZ=0 EndX=25.2 EndY=2.8 EndZ=0
    g49: Circle [constr] CenterX=95.6 CenterY=-57.3 CenterZ=0 NormalX=-1e-16 NormalY=0 NormalZ=1 AngleXU=-1.5708 Radius=1.1
    g50: ArcOfCircle [constr] CenterX=60.7 CenterY=-66.9 CenterZ=0 NormalX=-1e-16 NormalY=0 NormalZ=1 AngleXU=-3.14159 Radius=1.5 StartAngle=0 EndAngle=1.5708
    g51: LineSegment [constr] StartX=59.2 StartY=-66.1 StartZ=0 EndX=59.2 EndY=-66.9 EndZ=0
    g52: LineSegment [constr] StartX=51.15 StartY=-66.1 StartZ=0 EndX=59.2 EndY=-66.1 EndZ=0
    g53: LineSegment [constr] StartX=51.15 StartY=-67.6 StartZ=0 EndX=51.15 EndY=-66.1 EndZ=0
    g54: LineSegment [constr] StartX=56.7 StartY=-67.6 StartZ=0 EndX=51.15 EndY=-67.6 EndZ=0
    g55: LineSegment [constr] StartX=56.7 StartY=-69.9 StartZ=0 EndX=56.7 EndY=-67.6 EndZ=0
    g56: LineSegment [constr] StartX=67.1 StartY=-69.9 StartZ=0 EndX=56.7 EndY=-69.9 EndZ=0
    g57: LineSegment [constr] StartX=67.1 StartY=-68.4 StartZ=0 EndX=67.1 EndY=-69.9 EndZ=0
    g58: LineSegment [constr] StartX=60.7 StartY=-68.4 StartZ=0 EndX=67.1 EndY=-68.4 EndZ=0
    g59: LineSegment [constr] StartX=62.7 StartY=-60 StartZ=0 EndX=27.8 EndY=-60 EndZ=0
    g60: LineSegment [constr] StartX=62.7 StartY=-57.6 StartZ=0 EndX=62.7 EndY=-60 EndZ=0
    g61: LineSegment [constr] StartX=27.8 StartY=-57.6 StartZ=0 EndX=62.7 EndY=-57.6 EndZ=0
    g62: LineSegment [constr] StartX=27.8 StartY=-60 StartZ=0 EndX=27.8 EndY=-57.6 EndZ=0
    g63: Circle [constr] CenterX=-14 CenterY=-73.8 CenterZ=0 NormalX=-1e-16 NormalY=0 NormalZ=1 AngleXU=-1.5708 Radius=1.1
    g64: LineSegment [constr] StartX=-14.8 StartY=-64.1 StartZ=0 EndX=-16.4 EndY=-64.1 EndZ=0
    g65: LineSegment [constr] StartX=-14.8 StartY=-54 StartZ=0 EndX=-14.8 EndY=-64.1 EndZ=0
    g66: LineSegment [constr] StartX=-16.4 StartY=-54 StartZ=0 EndX=-14.8 EndY=-54 EndZ=0
    g67: LineSegment [constr] StartX=-16.4 StartY=-64.1 StartZ=0 EndX=-16.4 EndY=-54 EndZ=0
    g68: LineSegment [constr] StartX=52 StartY=-56.2 StartZ=0 EndX=27.8 EndY=-56.2 EndZ=0
    g69: LineSegment [constr] StartX=52 StartY=-53.8 StartZ=0 EndX=52 EndY=-56.2 EndZ=0
    g70: LineSegment [constr] StartX=27.8 StartY=-53.8 StartZ=0 EndX=52 EndY=-53.8 EndZ=0
    g71: LineSegment [constr] StartX=27.8 StartY=-56.2 StartZ=0 EndX=27.8 EndY=-53.8 EndZ=0
    g72: Circle [constr] CenterX=95.6 CenterY=-23.3 CenterZ=0 NormalX=-1e-16 NormalY=0 NormalZ=1 AngleXU=-1.5708 Radius=1.1
    g73: Circle [constr] CenterX=25.9 CenterY=0.6 CenterZ=0 NormalX=-1e-16 NormalY=0 NormalZ=1 AngleXU=-1.5708 Radius=1.1
    g74: Circle [constr] CenterX=25.9 CenterY=0.6 CenterZ=0 NormalX=0 NormalY=0 NormalZ=1 AngleXU=0 Radius=1.2
    g75: Circle [constr] CenterX=25.9 CenterY=0.6 CenterZ=0 NormalX=0 NormalY=0 NormalZ=1 AngleXU=0 Radius=1.2
    g76: Circle [constr] CenterX=95.6 CenterY=-23.3 CenterZ=0 NormalX=0 NormalY=0 NormalZ=1 AngleXU=0 Radius=1.1
    g77: Circle [constr] CenterX=95.6 CenterY=-57.3 CenterZ=0 NormalX=0 NormalY=0 NormalZ=1 AngleXU=0 Radius=1.1
    g78: Circle [constr] CenterX=-14 CenterY=-73.8 CenterZ=0 NormalX=0 NormalY=0 NormalZ=1 AngleXU=0 Radius=1.2
    g79: Circle CenterX=95.6 CenterY=-23.3 CenterZ=0 NormalX=0 NormalY=0 NormalZ=1 AngleXU=0 Radius=2.5
    g80: Circle CenterX=95.6 CenterY=-57.3 CenterZ=0 NormalX=0 NormalY=0 NormalZ=1 AngleXU=0 Radius=2.5
    g81: Circle CenterX=-14 CenterY=-73.8 CenterZ=0 NormalX=0 NormalY=0 NormalZ=1 AngleXU=0 Radius=2.5
    g82: Circle CenterX=25.9 CenterY=0.6 CenterZ=0 NormalX=0 NormalY=0 NormalZ=1 AngleXU=0 Radius=2.5
  constraints (161):
    c: Coincident(g34,g35)
    c: Coincident(g35,g36)
    c: Coincident(g64,g67)
    c: Coincident(g66,g67)
    c: Coincident(g37,g38)
    c: Coincident(g36,g37)
    c: Coincident(g64,g65)
    c: Coincident(g65,g66)
    c: Coincident(g38,g39)
    c: Coincident(g39,g40)
    c: Coincident(g33,g34)
    c: Coincident(g32,g33)
    c: Coincident(g41,g42)
    c: Coincident(g40,g41)
    c: Coincident(g42,g43)
    c: Coincident(g43,g44)
    c: Coincident(g31,g32)
    c: Coincident(g44,g45)
    c: Coincident(g45,g46)
    c: Coincident(g46,g47)
    c: Coincident(g30,g31)
    c: Coincident(g47,g48)
    c: Coincident(g59,g62)
    c: Coincident(g61,g62)
    c: Coincident(g68,g71)
    c: Coincident(g70,g71)
    c: Coincident(g29,g30)
    c: Coincident(g28,g29)
    c: Coincident(g27,g28)
    c: Coincident(g26,g27)
    c: Coincident(g2,g48)
    c: Coincident(g0,g2)
    c: Coincident(g22,g23)
    c: Coincident(g23,g24)
    c: Coincident(g0,g1)
    c: Coincident(g21,g22)
    c: Coincident(g24,g25)
    c: Coincident(g25,g26)
    c: Coincident(g53,g54)
    c: Coincident(g52,g53)
    c: Coincident(g68,g69)
    c: Coincident(g69,g70)
    c: Coincident(g55,g56)
    c: Coincident(g54,g55)
    c: Coincident(g50,g51)
    c: Coincident(g51,g52)
    c: Coincident(g1,g3)
    c: Coincident(g50,g58)
    c: Coincident(g4,g5)
    c: Coincident(g3,g4)
    c: Coincident(g59,g60)
    c: Coincident(g60,g61)
    c: Coincident(g56,g57)
    c: Coincident(g57,g58)
    c: Coincident(g17,g18)
    c: Coincident(g16,g17)
    c: Coincident(g20,g21)
    c: Coincident(g19,g20)
    c: Coincident(g18,g19)
    c: Coincident(g5,g6)
    c: Coincident(g14,g15)
    c: Coincident(g15,g16)
    c: Coincident(g7,g8)
    c: Coincident(g6,g7)
    c: Coincident(g13,g14)
    c: Coincident(g12,g13)
    c: Coincident(g8,g9)
    c: Coincident(g11,g12)
    c: Coincident(g10,g11)
    c: Coincident(g9,g10)
    c: Block(g0)
    c: Block(g1)
    c: Block(g2)
    c: Block(g3)
    c: Block(g4)
    c: Block(g5)
    c: Block(g6)
    c: Block(g7)
    c: Block(g8)
    c: Block(g9)
    c: Block(g10)
    c: Block(g11)
    c: Block(g12)
    c: Block(g13)
    c: Block(g14)
    c: Block(g15)
    c: Block(g16)
    c: Block(g17)
    c: Block(g18)
    c: Block(g19)
    c: Block(g20)
    c: Block(g21)
    c: Block(g22)
    c: Block(g23)
    c: Block(g24)
    c: Block(g25)
    c: Block(g26)
    c: Block(g27)
    c: Block(g28)
    c: Block(g29)
    c: Block(g30)
    c: Block(g31)
    c: Block(g32)
    c: Block(g33)
    c: Block(g34)
    c: Block(g35)
    c: Block(g36)
    c: Block(g37)
    c: Block(g38)
    c: Block(g39)
    c: Block(g40)
    c: Block(g41)
    c: Block(g42)
    c: Block(g43)
    c: Block(g44)
    c: Block(g45)
    c: Block(g46)
    c: Block(g47)
    c: Block(g48)
    c: Block(g49)
    c: Block(g50)
    c: Block(g51)
    c: Block(g52)
    c: Block(g53)
    c: Block(g54)
    c: Block(g55)
    c: Block(g56)
    c: Block(g57)
    c: Block(g58)
    c: Block(g59)
    c: Block(g60)
    c: Block(g61)
    c: Block(g62)
    c: Block(g63)
    c: Block(g64)
    c: Block(g65)
    c: Block(g66)
    c: Block(g67)
    c: Block(g68)
    c: Block(g69)
    c: Block(g70)
    c: Block(g71)
    c: Block(g72)
    c: Block(g73)
    c: Diameter(g75) = 2.4
    c: Coincident(g75,g74)
    c: Equal(g75,g74)
    c: Coincident(g76,g72)
    c: Equal(g76,g72)
    c: Coincident(g77,g49)
    c: Equal(g77,g49)
    c: Diameter(g78) = 2.4
    c: Coincident(g78,g63)
    c: Diameter(g79) = 5
    c: Coincident(g79,g72)
    c: Diameter(g80) = 5
    c: Coincident(g80,g49)
    c: Diameter(g81) = 5
    c: Coincident(g81,g63)
    c: Diameter(g82) = 5
    c: Coincident(g82,g73)
FEATURE [PartDesign::Pocket] Pocket017
  BaseFeature = -> Fillet005
  Direction = (0,0,-1)
  Length = 5
  Length2 = 5
  Profile = -> Sketch035
  ReferenceAxis = -> Sketch035 [N_Axis]
  Refine = true
  Suppressed = false
  Type = 0
FEATURE [PartDesign::Pocket] Pocket016
  BaseFeature = -> Pocket017
  Direction = (0,0,-1)
  Length = 0.5
  Length2 = 5
  Profile = -> Sketch034
  ReferenceAxis = -> Sketch034 [N_Axis]
  Refine = true
  Suppressed = false
  Type = 0
FEATURE [Sketcher::SketchObject] Sketch036
  ArcFitTolerance = 1e-06
  AttachmentOffset = pos=(0,0,-3.9) rot=(0,0,1;0rad)
  AttachmentSupport = -> [XY_Plane005]
  FullyConstrained = false
  MakeInternals = false
  MapMode = 5
  Placement = pos=(0,0,-3.9) rot=(0,0,1;0rad)
  sketch-geometry (12):
    g0: LineSegment [constr] StartX=25 StartY=-61.158 StartZ=0 EndX=25 EndY=-92.8827 EndZ=0
    g1: LineSegment [constr] StartX=25 StartY=-92.8827 StartZ=0 EndX=76 EndY=-92.8827 EndZ=0
    g2: LineSegment [constr] StartX=76 StartY=-92.8827 StartZ=0 EndX=76 EndY=-74.6 EndZ=0
    g3: LineSegment [constr] StartX=76 StartY=-74.6 StartZ=0 EndX=81.7754 EndY=-74.6 EndZ=0
    g4: LineSegment [constr] StartX=81.7754 StartY=-74.6 StartZ=0 EndX=81.7754 EndY=-61.158 EndZ=0
    g5: LineSegment [constr] StartX=81.7754 StartY=-61.158 StartZ=0 EndX=25 EndY=-61.158 EndZ=0
    g6: LineSegment StartX=25 StartY=-61.158 StartZ=0 EndX=25 EndY=-86.4525 EndZ=0
    g7: LineSegment StartX=25 StartY=-86.4525 StartZ=0 EndX=59.3 EndY=-86.4525 EndZ=0
    g8: LineSegment StartX=59.3 StartY=-86.4525 StartZ=0 EndX=59.3 EndY=-68.7 EndZ=0
    g9: LineSegment StartX=59.3 StartY=-68.7 StartZ=0 EndX=63.7 EndY=-68.7 EndZ=0
    g10: LineSegment StartX=63.7 StartY=-68.7 StartZ=0 EndX=63.7 EndY=-61.158 EndZ=0
    g11: LineSegment StartX=63.7 StartY=-61.158 StartZ=0 EndX=25 EndY=-61.158 EndZ=0
  constraints (31):
    c: Vertical(g0)
    c: Coincident(g0,g1)
    c: Horizontal(g1)
    c: Coincident(g1,g2)
    c: Vertical(g2)
    c: Coincident(g2,g3)
    c: Horizontal(g3)
    c: Coincident(g3,g4)
    c: Vertical(g4)
    c: Coincident(g4,g5)
    c: Coincident(g5,g0)
    c: Horizontal(g5)
    c: DistanceY(g3,g-1) = 74.6
    c: DistanceX(g-1,g1) = 76
    c: DistanceX(g-1,g0) = 25
    c: Coincident(g0,g6)
    c: PointOnObject(g6,g0)
    c: Coincident(g6,g7)
    c: Horizontal(g7)
    c: Coincident(g7,g8)
    c: Vertical(g8)
    c: Coincident(g8,g9)
    c: Horizontal(g9)
    c: Coincident(g9,g10)
    c: PointOnObject(g10,g5)
    c: Vertical(g10)
    c: Coincident(g10,g11)
    c: Coincident(g11,g6)
    c: DistanceX(g-1,g10) = 63.7
    c: DistanceY(g9,g-1) = 68.7
    c: DistanceX(g-1,g8) = 59.3
FEATURE [PartDesign::Pocket] Pocket018
  BaseFeature = -> Pocket016
  Direction = (0,0,-1)
  Length = 10
  Length2 = 5
  Profile = -> Sketch036
  ReferenceAxis = -> Sketch036 [N_Axis]
  Refine = true
  Reversed = true
  Suppressed = false
  Type = 0
FEATURE [PartDesign::Fillet] Fillet006
  Base = -> Pocket018 [Edge79,Edge81]
  BaseFeature = -> Pocket018
  Radius = 2
  Refine = true
  SupportTransform = false
  Suppressed = false
  UseAllEdges = false
FEATURE [PartDesign::Fillet] Fillet007
  Base = -> Fillet006 [Edge114,Edge132]
  BaseFeature = -> Fillet006
  Radius = 0.5
  Refine = true
  SupportTransform = false
  Suppressed = false
  UseAllEdges = false
FEATURE [Sketcher::SketchObject] Sketch038
  ArcFitTolerance = 1e-06
  AttachmentOffset = pos=(0,0,-5.1) rot=(0,0,1;0rad)
  AttachmentSupport = -> [XY_Plane005]
  FullyConstrained = true
  MakeInternals = false
  MapMode = 5
  Placement = pos=(0,0,-5.1) rot=(0,0,1;0rad)
  sketch-geometry (5):
    g0: LineSegment [constr] StartX=-8.14984 StartY=-81.2146 StartZ=0 EndX=-10.9689 EndY=-82.2406 EndZ=0
    g1: LineSegment StartX=-10.9689 StartY=-82.2406 StartZ=0 EndX=-10.3191 EndY=-84.0261 EndZ=0
    g2: LineSegment StartX=-10.3191 StartY=-84.0261 StartZ=0 EndX=-7.5 EndY=-83 EndZ=0
    g3: LineSegment StartX=-7.5 StartY=-83 StartZ=0 EndX=-8.14984 EndY=-81.2146 EndZ=0
    g4: ArcOfCircle CenterX=-9.55938 CenterY=-81.7276 CenterZ=0 NormalX=0 NormalY=0 NormalZ=1 AngleXU=0 Radius=1.5 StartAngle=0.349066 EndAngle=3.49066
  constraints (15):
    c: Coincident(g0,g1)
    c: Coincident(g1,g2)
    c: Coincident(g2,g3)
    c: Coincident(g3,g0)
    c: DistanceX(g2,g-1) = 7.5
    c: DistanceY(g2,g-1) = 83
    c: Perpendicular(g1,g2)
    c: Perpendicular(g0,g1)
    c: Perpendicular(g3,g0)
    c: Angle(g-1,g2) = 0.349066
    c: Distance(g3,g3) = 1.9
    c: Distance(g2,g2) = 3
    c: Coincident(g4,g0)
    c: PointOnObject(g4,g0)
    c: Coincident(g4,g0)
FEATURE [PartDesign::Pocket] Pocket020
  BaseFeature = -> Fillet007
  Direction = (0,0,-1)
  Length = 5
  Length2 = 2.4
  Profile = -> Sketch038
  ReferenceAxis = -> Sketch038 [N_Axis]
  Refine = true
  Suppressed = false
  Type = 4
FEATURE [PartDesign::Fillet] Fillet010
  Base = -> Pocket020 [Edge47,Edge49]
  BaseFeature = -> Pocket020
  Radius = 1
  Refine = true
  SupportTransform = false
  Suppressed = false
  UseAllEdges = false
FEATURE [PartDesign::Fillet] Fillet008
  Base = -> Fillet010 [Face6,Edge75,Face2,Face51]
  BaseFeature = -> Fillet010
  Radius = 0.299
  Refine = true
  SupportTransform = false
  Suppressed = false
  UseAllEdges = false
FEATURE [PartDesign::Body] Body002  label="case-trackball"
  AllowCompound = false
  Group = -> [Sketch028,Sketch030,Sketch029,Pad011,Sketch031,Pocket013,Sketch032,Pocket014,Sketch033,Pocket015,Sketch034,Fillet004,Fillet005,Sketch035,Pocket017,Pocket016,Sketch036,Pocket018,Fillet006,Fillet007,Sketch038,Pocket020,Fillet010,Fillet008]
  Origin = -> Origin005
  Tip = -> Fillet008
COMPONENT P4 — geometry summary ("torabo-tsuki-lp-XS-left 1"; no construction recipe available for this part):
  bounding box: 120.0 x 86.8 x 7.3 mm
  tessellated surface: 5,336 triangles
  volume: 14364 mm^3 (19% of its bounding box)
PROVENANCE & LICENSES
A FreeCAD (.FCStd) document from a public repository crawl; recipes are the document's own serialized feature recipes (and, for linked parts, companion documents' recipes).
License: other.
